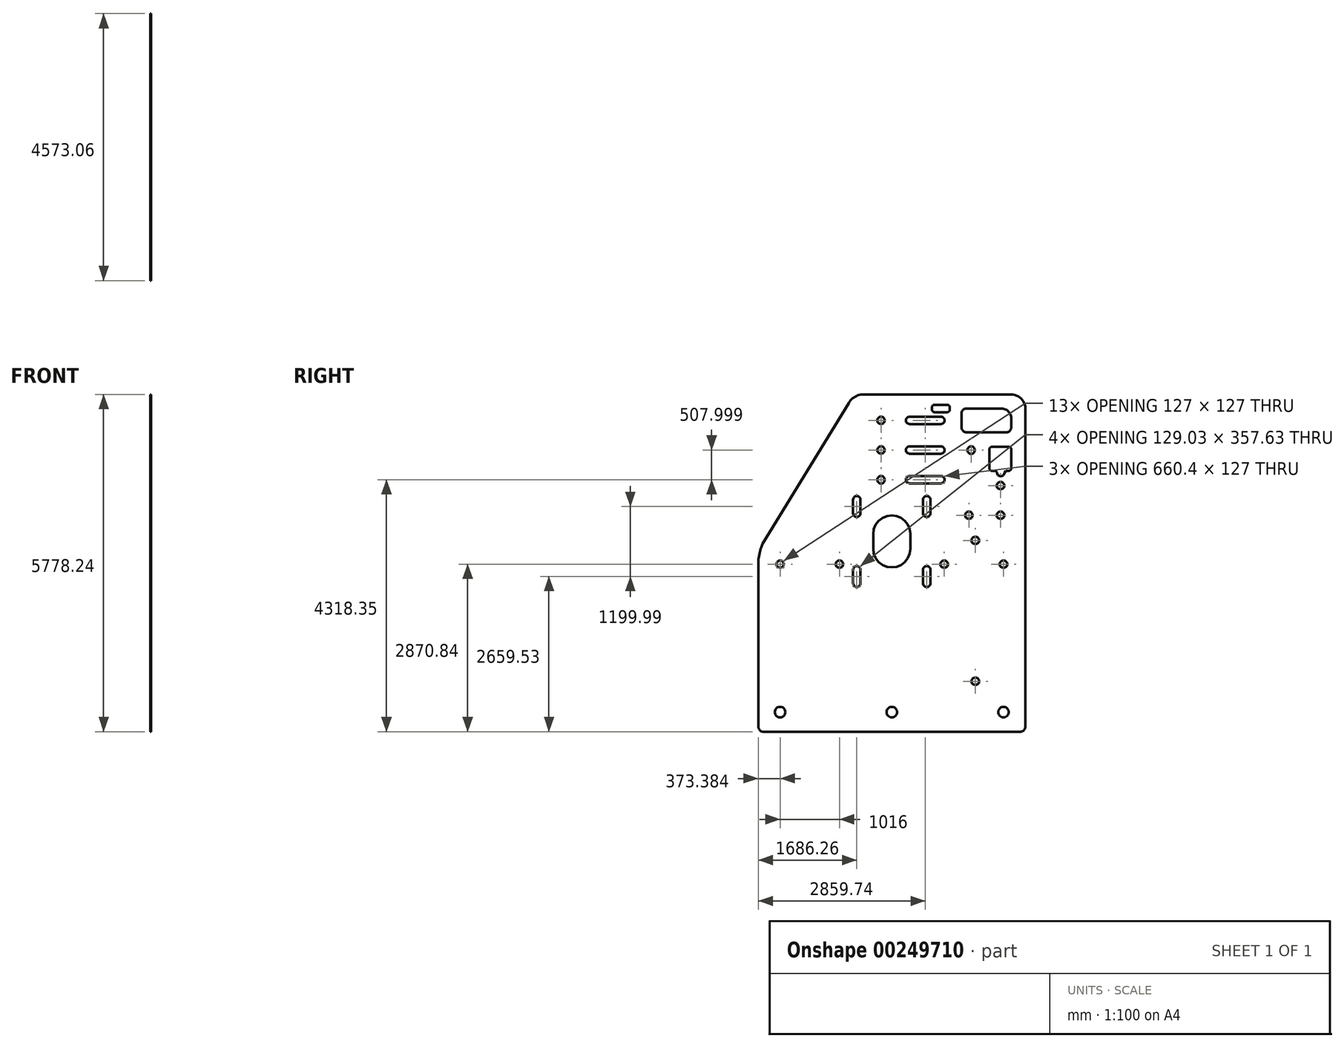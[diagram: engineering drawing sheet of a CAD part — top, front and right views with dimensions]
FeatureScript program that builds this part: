
annotation { "Feature Type Name" : "Feature", "Feature Type Description" : "" }
export const myFeature = defineFeature(function(context is Context, id is Id, definition is map)
    precondition{}
    {
        {
            var Q0;
            Q0=qCreatedBy(makeId("Right.planeOp"),FACE);
            var sketch = newSketch(context, id + "F0", { "sketchPlane" : qUnion([Q0])});
            skLineSegment(sketch, "E0", {"start": v(-705.3, 6120.73) * mm, "end": v(-698.95, 6105.42) * mm});
            skLineSegment(sketch, "E1", {"start": v(-603.87, 3290.42) * mm, "end": v(-593.78, 3277.27) * mm});
            skLineSegment(sketch, "E2", {"start": v(-617.02, 3190.53) * mm, "end": v(-632.33, 3184.18) * mm});
            skLineSegment(sketch, "E3", {"start": v(-648.77, 3182.02) * mm, "end": v(-665.2, 3184.18) * mm});
            skLineSegment(sketch, "E4", {"start": v(-593.78, 3277.27) * mm, "end": v(-587.43, 3261.96) * mm});
            skLineSegment(sketch, "E5", {"start": v(-665.2, 3306.86) * mm, "end": v(-648.77, 3309.02) * mm});
            skLineSegment(sketch, "E6", {"start": v(-710.1, 3229.09) * mm, "end": v(-712.27, 3245.52) * mm});
            skLineSegment(sketch, "E7", {"start": v(-2264.44, 6760.96) * mm, "end": v(-2248, 6758.8) * mm});
            skLineSegment(sketch, "E8", {"start": v(-2248, 6758.8) * mm, "end": v(-2232.7, 6752.45) * mm});
            skLineSegment(sketch, "E9", {"start": v(-693.67, 3290.42) * mm, "end": v(-680.52, 3300.51) * mm});
            skLineSegment(sketch, "E10", {"start": v(-710.1, 3261.96) * mm, "end": v(-703.76, 3277.27) * mm});
            skLineSegment(sketch, "E11", {"start": v(-603.87, 3200.62) * mm, "end": v(-617.02, 3190.53) * mm});
            skLineSegment(sketch, "E12", {"start": v(-617.02, 3300.51) * mm, "end": v(-603.87, 3290.42) * mm});
            skLineSegment(sketch, "E13", {"start": v(-648.77, 3309.02) * mm, "end": v(-632.33, 3306.86) * mm});
            skLineSegment(sketch, "E14", {"start": v(-2232.7, 6752.45) * mm, "end": v(-2219.54, 6742.36) * mm});
            skLineSegment(sketch, "E15", {"start": v(-665.2, 3184.18) * mm, "end": v(-680.52, 3190.53) * mm});
            skLineSegment(sketch, "E16", {"start": v(-2325.78, 6713.9) * mm, "end": v(-2319.44, 6729.2) * mm});
            skLineSegment(sketch, "E17", {"start": v(-2264.44, 6633.96) * mm, "end": v(-2280.88, 6636.12) * mm});
            skLineSegment(sketch, "E18", {"start": v(-2203.1, 6713.9) * mm, "end": v(-2200.94, 6697.46) * mm});
            skLineSegment(sketch, "E19", {"start": v(-693.67, 3200.62) * mm, "end": v(-703.76, 3213.77) * mm});
            skLineSegment(sketch, "E20", {"start": v(-2219.54, 6742.36) * mm, "end": v(-2209.45, 6729.2) * mm});
            skLineSegment(sketch, "E21", {"start": v(-2325.78, 6681.02) * mm, "end": v(-2327.94, 6697.46) * mm});
            skLineSegment(sketch, "E22", {"start": v(-585.27, 3245.52) * mm, "end": v(-587.43, 3229.09) * mm});
            skLineSegment(sketch, "E23", {"start": v(-2309.35, 6652.56) * mm, "end": v(-2319.44, 6665.7) * mm});
            skLineSegment(sketch, "E24", {"start": v(-2232.7, 6642.47) * mm, "end": v(-2248, 6636.12) * mm});
            skLineSegment(sketch, "E25", {"start": v(-698.95, 6105.42) * mm, "end": v(-696.79, 6088.98) * mm});
            skLineSegment(sketch, "E26", {"start": v(-680.52, 3190.53) * mm, "end": v(-693.67, 3200.62) * mm});
            skLineSegment(sketch, "E27", {"start": v(-703.76, 3277.27) * mm, "end": v(-693.67, 3290.42) * mm});
            skLineSegment(sketch, "E28", {"start": v(-587.43, 3261.96) * mm, "end": v(-585.27, 3245.52) * mm});
            skLineSegment(sketch, "E29", {"start": v(-632.33, 3306.86) * mm, "end": v(-617.02, 3300.51) * mm});
            skLineSegment(sketch, "E30", {"start": v(-712.27, 3245.52) * mm, "end": v(-710.1, 3261.96) * mm});
            skLineSegment(sketch, "E31", {"start": v(-2209.45, 6729.2) * mm, "end": v(-2203.1, 6713.9) * mm});
            skLineSegment(sketch, "E32", {"start": v(-703.76, 3213.77) * mm, "end": v(-710.1, 3229.09) * mm});
            skLineSegment(sketch, "E33", {"start": v(-680.52, 3300.51) * mm, "end": v(-665.2, 3306.86) * mm});
            skLineSegment(sketch, "E34", {"start": v(-587.43, 3229.09) * mm, "end": v(-593.78, 3213.77) * mm});
            skLineSegment(sketch, "E35", {"start": v(-632.33, 3184.18) * mm, "end": v(-648.77, 3182.02) * mm});
            skLineSegment(sketch, "E36", {"start": v(-2203.1, 6681.02) * mm, "end": v(-2209.45, 6665.7) * mm});
            skLineSegment(sketch, "E37", {"start": v(-660.44, 7189.1) * mm, "end": v(-666.79, 7173.79) * mm});
            skLineSegment(sketch, "E38", {"start": v(-783.12, 7221.97) * mm, "end": v(-776.77, 7237.29) * mm});
            skLineSegment(sketch, "E39", {"start": v(-2280.88, 6758.8) * mm, "end": v(-2264.44, 6760.96) * mm});
            skLineSegment(sketch, "E40", {"start": v(-676.88, 7250.44) * mm, "end": v(-666.79, 7237.29) * mm});
            skLineSegment(sketch, "E41", {"start": v(-753.53, 7150.55) * mm, "end": v(-766.68, 7160.64) * mm});
            skLineSegment(sketch, "E42", {"start": v(-721.78, 7269.04) * mm, "end": v(-705.34, 7266.88) * mm});
            skLineSegment(sketch, "E43", {"start": v(-776.77, 7173.79) * mm, "end": v(-783.12, 7189.1) * mm});
            skLineSegment(sketch, "E44", {"start": v(-738.21, 7266.88) * mm, "end": v(-721.78, 7269.04) * mm});
            skLineSegment(sketch, "E45", {"start": v(-2296.2, 6752.45) * mm, "end": v(-2280.88, 6758.8) * mm});
            skLineSegment(sketch, "E46", {"start": v(-2319.44, 6665.7) * mm, "end": v(-2325.78, 6681.02) * mm});
            skLineSegment(sketch, "E47", {"start": v(-2248, 6636.12) * mm, "end": v(-2264.44, 6633.96) * mm});
            skLineSegment(sketch, "E48", {"start": v(-666.79, 7173.79) * mm, "end": v(-676.88, 7160.64) * mm});
            skLineSegment(sketch, "E49", {"start": v(-271.96, 6057.23) * mm, "end": v(-278.3, 6072.55) * mm});
            skLineSegment(sketch, "E50", {"start": v(-766.68, 7250.44) * mm, "end": v(-753.53, 7260.53) * mm});
            skLineSegment(sketch, "E51", {"start": v(-2296.2, 6642.47) * mm, "end": v(-2309.35, 6652.56) * mm});
            skLineSegment(sketch, "E52", {"start": v(-2309.35, 6742.36) * mm, "end": v(-2296.2, 6752.45) * mm});
            skLineSegment(sketch, "E53", {"start": v(-2219.54, 6652.56) * mm, "end": v(-2232.7, 6642.47) * mm});
            skLineSegment(sketch, "E54", {"start": v(-2280.88, 6636.12) * mm, "end": v(-2296.2, 6642.47) * mm});
            skLineSegment(sketch, "E55", {"start": v(-705.34, 7144.2) * mm, "end": v(-721.78, 7142.04) * mm});
            skLineSegment(sketch, "E56", {"start": v(-783.12, 7189.1) * mm, "end": v(-785.28, 7205.54) * mm});
            skLineSegment(sketch, "E57", {"start": v(-660.44, 7221.97) * mm, "end": v(-658.28, 7205.54) * mm});
            skLineSegment(sketch, "E58", {"start": v(-2327.94, 6697.46) * mm, "end": v(-2325.78, 6713.9) * mm});
            skLineSegment(sketch, "E59", {"start": v(-776.77, 7237.29) * mm, "end": v(-766.68, 7250.44) * mm});
            skLineSegment(sketch, "E60", {"start": v(-666.79, 7237.29) * mm, "end": v(-660.44, 7221.97) * mm});
            skLineSegment(sketch, "E61", {"start": v(-690.03, 7150.55) * mm, "end": v(-705.34, 7144.2) * mm});
            skLineSegment(sketch, "E62", {"start": v(-2209.45, 6665.7) * mm, "end": v(-2219.54, 6652.56) * mm});
            skLineSegment(sketch, "E63", {"start": v(-676.88, 7160.64) * mm, "end": v(-690.03, 7150.55) * mm});
            skLineSegment(sketch, "E64", {"start": v(-785.28, 7205.54) * mm, "end": v(-783.12, 7221.97) * mm});
            skLineSegment(sketch, "E65", {"start": v(-233.4, 6150.32) * mm, "end": v(-216.97, 6152.48) * mm});
            skLineSegment(sketch, "E66", {"start": v(-2319.44, 6729.2) * mm, "end": v(-2309.35, 6742.36) * mm});
            skLineSegment(sketch, "E67", {"start": v(-2200.94, 6697.46) * mm, "end": v(-2203.1, 6681.02) * mm});
            skLineSegment(sketch, "E68", {"start": v(-658.28, 7205.54) * mm, "end": v(-660.44, 7189.1) * mm});
            skLineSegment(sketch, "E69", {"start": v(-280.47, 6088.98) * mm, "end": v(-278.3, 6105.42) * mm});
            skLineSegment(sketch, "E70", {"start": v(-261.87, 6044.08) * mm, "end": v(-271.96, 6057.23) * mm});
            skLineSegment(sketch, "E71", {"start": v(-216.97, 6152.48) * mm, "end": v(-200.53, 6150.32) * mm});
            skLineSegment(sketch, "E72", {"start": v(-153.47, 6088.98) * mm, "end": v(-155.63, 6072.55) * mm});
            skLineSegment(sketch, "E73", {"start": v(-155.63, 6072.55) * mm, "end": v(-161.98, 6057.23) * mm});
            skLineSegment(sketch, "E74", {"start": v(-766.68, 7160.64) * mm, "end": v(-776.77, 7173.79) * mm});
            skLineSegment(sketch, "E75", {"start": v(-161.98, 6120.73) * mm, "end": v(-155.63, 6105.42) * mm});
            skLineSegment(sketch, "E76", {"start": v(-738.21, 7144.2) * mm, "end": v(-753.53, 7150.55) * mm});
            skLineSegment(sketch, "E77", {"start": v(-278.3, 6072.55) * mm, "end": v(-280.47, 6088.98) * mm});
            skLineSegment(sketch, "E78", {"start": v(-278.3, 6105.42) * mm, "end": v(-271.96, 6120.73) * mm});
            skLineSegment(sketch, "E79", {"start": v(-248.72, 6034) * mm, "end": v(-261.87, 6044.08) * mm});
            skLineSegment(sketch, "E80", {"start": v(-248.72, 6143.98) * mm, "end": v(-233.4, 6150.32) * mm});
            skLineSegment(sketch, "E81", {"start": v(-216.97, 6533.48) * mm, "end": v(-233.4, 6535.65) * mm});
            skLineSegment(sketch, "E82", {"start": v(-155.63, 6105.42) * mm, "end": v(-153.47, 6088.98) * mm});
            skLineSegment(sketch, "E83", {"start": v(-161.98, 6057.23) * mm, "end": v(-172.07, 6044.08) * mm});
            skLineSegment(sketch, "E84", {"start": v(-185.22, 6034) * mm, "end": v(-200.53, 6027.65) * mm});
            skLineSegment(sketch, "E85", {"start": v(-721.78, 7142.04) * mm, "end": v(-738.21, 7144.2) * mm});
            skLineSegment(sketch, "E86", {"start": v(-185.22, 6542) * mm, "end": v(-200.53, 6535.65) * mm});
            skLineSegment(sketch, "E87", {"start": v(-172.07, 6552.08) * mm, "end": v(-185.22, 6542) * mm});
            skLineSegment(sketch, "E88", {"start": v(-200.53, 6027.65) * mm, "end": v(-216.97, 6025.48) * mm});
            skLineSegment(sketch, "E89", {"start": v(-233.4, 6027.65) * mm, "end": v(-248.72, 6034) * mm});
            skLineSegment(sketch, "E90", {"start": v(-172.07, 6133.89) * mm, "end": v(-161.98, 6120.73) * mm});
            skLineSegment(sketch, "E91", {"start": v(-200.53, 6535.65) * mm, "end": v(-216.97, 6533.48) * mm});
            skLineSegment(sketch, "E92", {"start": v(-172.07, 6044.08) * mm, "end": v(-185.22, 6034) * mm});
            skLineSegment(sketch, "E93", {"start": v(-753.53, 7260.53) * mm, "end": v(-738.21, 7266.88) * mm});
            skLineSegment(sketch, "E94", {"start": v(-261.87, 6133.89) * mm, "end": v(-248.72, 6143.98) * mm});
            skLineSegment(sketch, "E95", {"start": v(-690.03, 7260.53) * mm, "end": v(-676.88, 7250.44) * mm});
            skLineSegment(sketch, "E96", {"start": v(-705.34, 7266.88) * mm, "end": v(-690.03, 7260.53) * mm});
            skLineSegment(sketch, "E97", {"start": v(-200.53, 6150.32) * mm, "end": v(-185.22, 6143.98) * mm});
            skLineSegment(sketch, "E98", {"start": v(-185.22, 6651.98) * mm, "end": v(-172.07, 6641.89) * mm});
            skLineSegment(sketch, "E99", {"start": v(-261.87, 6641.89) * mm, "end": v(-248.72, 6651.98) * mm});
            skLineSegment(sketch, "E100", {"start": v(-172.07, 6641.89) * mm, "end": v(-161.98, 6628.73) * mm});
            skLineSegment(sketch, "E101", {"start": v(-44.72, 7552.16) * mm, "end": v(-50.51, 7543.5) * mm});
            skLineSegment(sketch, "E102", {"start": v(-261.87, 6552.08) * mm, "end": v(-271.96, 6565.23) * mm});
            skLineSegment(sketch, "E103", {"start": v(-216.97, 6660.48) * mm, "end": v(-200.53, 6658.32) * mm});
            skLineSegment(sketch, "E104", {"start": v(-50.51, 7543.5) * mm, "end": v(-57.38, 7535.66) * mm});
            skLineSegment(sketch, "E105", {"start": v(-216.97, 6025.48) * mm, "end": v(-233.4, 6027.65) * mm});
            skLineSegment(sketch, "E106", {"start": v(-161.98, 6628.73) * mm, "end": v(-155.63, 6613.42) * mm});
            skLineSegment(sketch, "E107", {"start": v(-83.23, 7518.4) * mm, "end": v(-93.1, 7515.05) * mm});
            skLineSegment(sketch, "E108", {"start": v(-271.96, 6628.73) * mm, "end": v(-261.87, 6641.89) * mm});
            skLineSegment(sketch, "E109", {"start": v(-153.47, 6596.98) * mm, "end": v(-155.63, 6580.55) * mm});
            skLineSegment(sketch, "E110", {"start": v(-103.31, 7513.01) * mm, "end": v(-113.7, 7512.33) * mm});
            skLineSegment(sketch, "E111", {"start": v(-113.7, 7512.33) * mm, "end": v(-805.3, 7512.33) * mm});
            skLineSegment(sketch, "E112", {"start": v(-40.12, 7561.5) * mm, "end": v(-44.72, 7552.16) * mm});
            skLineSegment(sketch, "E113", {"start": v(-161.98, 6565.23) * mm, "end": v(-172.07, 6552.08) * mm});
            skLineSegment(sketch, "E114", {"start": v(-65.22, 7528.8) * mm, "end": v(-73.88, 7523) * mm});
            skLineSegment(sketch, "E115", {"start": v(-36.77, 7571.37) * mm, "end": v(-40.12, 7561.5) * mm});
            skLineSegment(sketch, "E116", {"start": v(-271.96, 6565.23) * mm, "end": v(-278.3, 6580.55) * mm});
            skLineSegment(sketch, "E117", {"start": v(-73.88, 7523) * mm, "end": v(-83.23, 7518.4) * mm});
            skLineSegment(sketch, "E118", {"start": v(-155.63, 6613.42) * mm, "end": v(-153.47, 6596.98) * mm});
            skLineSegment(sketch, "E119", {"start": v(-34.73, 7581.59) * mm, "end": v(-36.77, 7571.37) * mm});
            skLineSegment(sketch, "E120", {"start": v(-57.38, 7535.66) * mm, "end": v(-65.22, 7528.8) * mm});
            skLineSegment(sketch, "E121", {"start": v(-200.53, 6658.32) * mm, "end": v(-185.22, 6651.98) * mm});
            skLineSegment(sketch, "E122", {"start": v(-155.63, 6580.55) * mm, "end": v(-161.98, 6565.23) * mm});
            skLineSegment(sketch, "E123", {"start": v(-248.72, 6651.98) * mm, "end": v(-233.4, 6658.32) * mm});
            skLineSegment(sketch, "E124", {"start": v(-93.1, 7515.05) * mm, "end": v(-103.31, 7513.01) * mm});
            skLineSegment(sketch, "E125", {"start": v(-233.4, 6658.32) * mm, "end": v(-216.97, 6660.48) * mm});
            skLineSegment(sketch, "E126", {"start": v(-185.22, 6143.98) * mm, "end": v(-172.07, 6133.89) * mm});
            skLineSegment(sketch, "E127", {"start": v(-248.72, 6542) * mm, "end": v(-261.87, 6552.08) * mm});
            skLineSegment(sketch, "E128", {"start": v(-233.4, 6535.65) * mm, "end": v(-248.72, 6542) * mm});
            skLineSegment(sketch, "E129", {"start": v(-278.3, 6613.42) * mm, "end": v(-271.96, 6628.73) * mm});
            skLineSegment(sketch, "E130", {"start": v(-280.47, 6596.98) * mm, "end": v(-278.3, 6613.42) * mm});
            skLineSegment(sketch, "E131", {"start": v(-278.3, 6580.55) * mm, "end": v(-280.47, 6596.98) * mm});
            skLineSegment(sketch, "E132", {"start": v(-34.05, 7749.15) * mm, "end": v(-34.05, 7591.99) * mm});
            skLineSegment(sketch, "E133", {"start": v(-46.9, 7813.78) * mm, "end": v(-39.8, 7792.87) * mm});
            skLineSegment(sketch, "E134", {"start": v(-56.68, 7833.6) * mm, "end": v(-46.9, 7813.78) * mm});
            skLineSegment(sketch, "E135", {"start": v(-874.28, 7552.16) * mm, "end": v(-868.5, 7543.5) * mm});
            skLineSegment(sketch, "E136", {"start": v(-34.05, 7591.99) * mm, "end": v(-34.73, 7581.59) * mm});
            skLineSegment(sketch, "E137", {"start": v(-868.5, 7886.88) * mm, "end": v(-861.62, 7894.71) * mm});
            skLineSegment(sketch, "E138", {"start": v(-853.79, 7901.58) * mm, "end": v(-845.13, 7907.37) * mm});
            skLineSegment(sketch, "E139", {"start": v(-118.5, 7895.42) * mm, "end": v(-100.13, 7883.14) * mm});
            skLineSegment(sketch, "E140", {"start": v(-868.5, 7543.5) * mm, "end": v(-861.62, 7535.66) * mm});
            skLineSegment(sketch, "E141", {"start": v(-882.24, 7859) * mm, "end": v(-878.89, 7868.87) * mm});
            skLineSegment(sketch, "E142", {"start": v(-835.78, 7518.4) * mm, "end": v(-825.91, 7515.05) * mm});
            skLineSegment(sketch, "E143", {"start": v(-825.91, 7515.05) * mm, "end": v(-815.7, 7513.01) * mm});
            skLineSegment(sketch, "E144", {"start": v(-815.7, 7513.01) * mm, "end": v(-805.3, 7512.33) * mm});
            skLineSegment(sketch, "E145", {"start": v(-138.31, 7905.19) * mm, "end": v(-118.5, 7895.42) * mm});
            skLineSegment(sketch, "E146", {"start": v(-845.13, 7907.37) * mm, "end": v(-835.78, 7911.98) * mm});
            skLineSegment(sketch, "E147", {"start": v(-83.52, 7868.58) * mm, "end": v(-68.95, 7851.97) * mm});
            skLineSegment(sketch, "E148", {"start": v(-35.5, 7771.2) * mm, "end": v(-34.05, 7749.15) * mm});
            skLineSegment(sketch, "E149", {"start": v(-853.79, 7528.8) * mm, "end": v(-845.13, 7523) * mm});
            skLineSegment(sketch, "E150", {"start": v(-202.94, 7918.04) * mm, "end": v(-180.9, 7916.6) * mm});
            skLineSegment(sketch, "E151", {"start": v(-861.62, 7535.66) * mm, "end": v(-853.79, 7528.8) * mm});
            skLineSegment(sketch, "E152", {"start": v(-68.95, 7851.97) * mm, "end": v(-56.68, 7833.6) * mm});
            skLineSegment(sketch, "E153", {"start": v(-884.95, 7591.99) * mm, "end": v(-884.95, 7838.39) * mm});
            skLineSegment(sketch, "E154", {"start": v(-815.7, 7917.36) * mm, "end": v(-805.3, 7918.04) * mm});
            skLineSegment(sketch, "E155", {"start": v(-100.13, 7883.14) * mm, "end": v(-83.52, 7868.58) * mm});
            skLineSegment(sketch, "E156", {"start": v(-825.91, 7915.33) * mm, "end": v(-815.7, 7917.36) * mm});
            skLineSegment(sketch, "E157", {"start": v(-878.89, 7868.87) * mm, "end": v(-874.28, 7878.21) * mm});
            skLineSegment(sketch, "E158", {"start": v(-180.9, 7916.6) * mm, "end": v(-159.23, 7912.29) * mm});
            skLineSegment(sketch, "E159", {"start": v(-845.13, 7523) * mm, "end": v(-835.78, 7518.4) * mm});
            skLineSegment(sketch, "E160", {"start": v(-884.95, 7838.39) * mm, "end": v(-884.27, 7848.78) * mm});
            skLineSegment(sketch, "E161", {"start": v(-861.62, 7894.71) * mm, "end": v(-853.79, 7901.58) * mm});
            skLineSegment(sketch, "E162", {"start": v(-159.23, 7912.29) * mm, "end": v(-138.31, 7905.19) * mm});
            skLineSegment(sketch, "E163", {"start": v(-805.3, 7918.04) * mm, "end": v(-202.94, 7918.04) * mm});
            skLineSegment(sketch, "E164", {"start": v(-712.27, 5658.52) * mm, "end": v(-710.1, 5674.96) * mm});
            skLineSegment(sketch, "E165", {"start": v(-39.8, 7792.87) * mm, "end": v(-35.5, 7771.2) * mm});
            skLineSegment(sketch, "E166", {"start": v(-835.78, 7911.98) * mm, "end": v(-825.91, 7915.33) * mm});
            skLineSegment(sketch, "E167", {"start": v(-693.67, 5703.42) * mm, "end": v(-680.52, 5713.51) * mm});
            skLineSegment(sketch, "E168", {"start": v(-603.87, 5613.62) * mm, "end": v(-617.02, 5603.53) * mm});
            skLineSegment(sketch, "E169", {"start": v(-632.33, 5719.86) * mm, "end": v(-617.02, 5713.51) * mm});
            skLineSegment(sketch, "E170", {"start": v(-665.2, 5597.18) * mm, "end": v(-680.52, 5603.53) * mm});
            skLineSegment(sketch, "E171", {"start": v(-710.1, 5642.09) * mm, "end": v(-712.27, 5658.52) * mm});
            skLineSegment(sketch, "E172", {"start": v(-703.76, 5626.77) * mm, "end": v(-710.1, 5642.09) * mm});
            skLineSegment(sketch, "E173", {"start": v(-878.89, 7561.5) * mm, "end": v(-874.28, 7552.16) * mm});
            skLineSegment(sketch, "E174", {"start": v(-617.02, 5603.53) * mm, "end": v(-632.33, 5597.18) * mm});
            skLineSegment(sketch, "E175", {"start": v(-710.1, 5674.96) * mm, "end": v(-703.76, 5690.27) * mm});
            skLineSegment(sketch, "E176", {"start": v(-665.2, 5719.86) * mm, "end": v(-648.77, 5722.02) * mm});
            skLineSegment(sketch, "E177", {"start": v(-648.77, 5595.02) * mm, "end": v(-665.2, 5597.18) * mm});
            skLineSegment(sketch, "E178", {"start": v(-884.27, 7581.59) * mm, "end": v(-882.24, 7571.37) * mm});
            skLineSegment(sketch, "E179", {"start": v(-874.28, 7878.21) * mm, "end": v(-868.5, 7886.88) * mm});
            skLineSegment(sketch, "E180", {"start": v(-882.24, 7571.37) * mm, "end": v(-878.89, 7561.5) * mm});
            skLineSegment(sketch, "E181", {"start": v(-593.78, 5690.27) * mm, "end": v(-587.43, 5674.96) * mm});
            skLineSegment(sketch, "E182", {"start": v(-587.43, 5642.09) * mm, "end": v(-593.78, 5626.77) * mm});
            skLineSegment(sketch, "E183", {"start": v(-587.43, 5674.96) * mm, "end": v(-585.27, 5658.52) * mm});
            skLineSegment(sketch, "E184", {"start": v(-632.33, 5597.18) * mm, "end": v(-648.77, 5595.02) * mm});
            skLineSegment(sketch, "E185", {"start": v(-884.27, 7848.78) * mm, "end": v(-882.24, 7859) * mm});
            skLineSegment(sketch, "E186", {"start": v(-680.52, 5603.53) * mm, "end": v(-693.67, 5613.62) * mm});
            skLineSegment(sketch, "E187", {"start": v(-680.52, 5713.51) * mm, "end": v(-665.2, 5719.86) * mm});
            skLineSegment(sketch, "E188", {"start": v(-648.77, 5722.02) * mm, "end": v(-632.33, 5719.86) * mm});
            skLineSegment(sketch, "E189", {"start": v(-585.27, 5658.52) * mm, "end": v(-587.43, 5642.09) * mm});
            skLineSegment(sketch, "E190", {"start": v(-617.02, 5713.51) * mm, "end": v(-603.87, 5703.42) * mm});
            skLineSegment(sketch, "E191", {"start": v(-884.95, 7591.99) * mm, "end": v(-884.27, 7581.59) * mm});
            skLineSegment(sketch, "E192", {"start": v(-593.78, 5626.77) * mm, "end": v(-603.87, 5613.62) * mm});
            skLineSegment(sketch, "E193", {"start": v(-693.67, 5613.62) * mm, "end": v(-703.76, 5626.77) * mm});
            skLineSegment(sketch, "E194", {"start": v(-603.87, 5703.42) * mm, "end": v(-593.78, 5690.27) * mm});
            skLineSegment(sketch, "E195", {"start": v(-703.76, 5690.27) * mm, "end": v(-693.67, 5703.42) * mm});
            skLineSegment(sketch, "E196", {"start": v(-2280.88, 7653.37) * mm, "end": v(-2296.2, 7659.72) * mm});
            skLineSegment(sketch, "E197", {"start": v(-2248, 7776.05) * mm, "end": v(-2232.7, 7769.7) * mm});
            skLineSegment(sketch, "E198", {"start": v(-2264.44, 7778.2) * mm, "end": v(-2248, 7776.05) * mm});
            skLineSegment(sketch, "E199", {"start": v(-2219.54, 7669.8) * mm, "end": v(-2232.7, 7659.72) * mm});
            skLineSegment(sketch, "E200", {"start": v(-2232.7, 7769.7) * mm, "end": v(-2219.54, 7759.6) * mm});
            skLineSegment(sketch, "E201", {"start": v(-2325.78, 7698.27) * mm, "end": v(-2327.94, 7714.7) * mm});
            skLineSegment(sketch, "E202", {"start": v(-2296.2, 7659.72) * mm, "end": v(-2309.35, 7669.8) * mm});
            skLineSegment(sketch, "E203", {"start": v(-2280.88, 7776.05) * mm, "end": v(-2264.44, 7778.2) * mm});
            skLineSegment(sketch, "E204", {"start": v(-2203.1, 7698.27) * mm, "end": v(-2209.45, 7682.96) * mm});
            skLineSegment(sketch, "E205", {"start": v(-2309.35, 7669.8) * mm, "end": v(-2319.44, 7682.96) * mm});
            skLineSegment(sketch, "E206", {"start": v(-2209.45, 7746.46) * mm, "end": v(-2203.1, 7731.14) * mm});
            skLineSegment(sketch, "E207", {"start": v(-2309.35, 7251.6) * mm, "end": v(-2296.2, 7261.7) * mm});
            skLineSegment(sketch, "E208", {"start": v(-2327.94, 7714.7) * mm, "end": v(-2325.78, 7731.14) * mm});
            skLineSegment(sketch, "E209", {"start": v(-2325.78, 7190.27) * mm, "end": v(-2327.94, 7206.7) * mm});
            skLineSegment(sketch, "E210", {"start": v(-2280.88, 7268.05) * mm, "end": v(-2264.44, 7270.2) * mm});
            skLineSegment(sketch, "E211", {"start": v(-2296.2, 7151.72) * mm, "end": v(-2309.35, 7161.8) * mm});
            skLineSegment(sketch, "E212", {"start": v(-2309.35, 7759.6) * mm, "end": v(-2296.2, 7769.7) * mm});
            skLineSegment(sketch, "E213", {"start": v(-2232.7, 7659.72) * mm, "end": v(-2248, 7653.37) * mm});
            skLineSegment(sketch, "E214", {"start": v(-2325.78, 7223.14) * mm, "end": v(-2319.44, 7238.46) * mm});
            skLineSegment(sketch, "E215", {"start": v(-2319.44, 7682.96) * mm, "end": v(-2325.78, 7698.27) * mm});
            skLineSegment(sketch, "E216", {"start": v(-2264.44, 7651.2) * mm, "end": v(-2280.88, 7653.37) * mm});
            skLineSegment(sketch, "E217", {"start": v(-2264.44, 7143.2) * mm, "end": v(-2280.88, 7145.37) * mm});
            skLineSegment(sketch, "E218", {"start": v(-2200.94, 7714.7) * mm, "end": v(-2203.1, 7698.27) * mm});
            skLineSegment(sketch, "E219", {"start": v(-2248, 7145.37) * mm, "end": v(-2264.44, 7143.2) * mm});
            skLineSegment(sketch, "E220", {"start": v(-2296.2, 7769.7) * mm, "end": v(-2280.88, 7776.05) * mm});
            skLineSegment(sketch, "E221", {"start": v(-2203.1, 7731.14) * mm, "end": v(-2200.94, 7714.7) * mm});
            skLineSegment(sketch, "E222", {"start": v(-2209.45, 7682.96) * mm, "end": v(-2219.54, 7669.8) * mm});
            skLineSegment(sketch, "E223", {"start": v(-2325.78, 7731.14) * mm, "end": v(-2319.44, 7746.46) * mm});
            skLineSegment(sketch, "E224", {"start": v(-2248, 7653.37) * mm, "end": v(-2264.44, 7651.2) * mm});
            skLineSegment(sketch, "E225", {"start": v(-2319.44, 7746.46) * mm, "end": v(-2309.35, 7759.6) * mm});
            skLineSegment(sketch, "E226", {"start": v(-2219.54, 7759.6) * mm, "end": v(-2209.45, 7746.46) * mm});
            skLineSegment(sketch, "E227", {"start": v(-2280.88, 7145.37) * mm, "end": v(-2296.2, 7151.72) * mm});
            skLineSegment(sketch, "E228", {"start": v(-2744.06, 6354.93) * mm, "end": v(-2741.87, 6371.62) * mm});
            skLineSegment(sketch, "E229", {"start": v(-1525.17, 6080.7) * mm, "end": v(-1535.43, 6094.07) * mm});
            skLineSegment(sketch, "E230", {"start": v(-1433.94, 6080.7) * mm, "end": v(-1447.3, 6070.45) * mm});
            skLineSegment(sketch, "E231", {"start": v(-2200.94, 7206.7) * mm, "end": v(-2203.1, 7190.27) * mm});
            skLineSegment(sketch, "E232", {"start": v(-2319.44, 7238.46) * mm, "end": v(-2309.35, 7251.6) * mm});
            skLineSegment(sketch, "E233", {"start": v(-2744.06, 5154.93) * mm, "end": v(-2741.87, 5171.63) * mm});
            skLineSegment(sketch, "E234", {"start": v(-1496.25, 6417.24) * mm, "end": v(-1479.55, 6419.44) * mm});
            skLineSegment(sketch, "E235", {"start": v(-1544.07, 6126.33) * mm, "end": v(-1544.07, 6354.93) * mm});
            skLineSegment(sketch, "E236", {"start": v(-1541.87, 4909.63) * mm, "end": v(-1544.07, 4926.33) * mm});
            skLineSegment(sketch, "E237", {"start": v(-2309.35, 7161.8) * mm, "end": v(-2319.44, 7174.96) * mm});
            skLineSegment(sketch, "E238", {"start": v(-2232.7, 7151.72) * mm, "end": v(-2248, 7145.37) * mm});
            skLineSegment(sketch, "E239", {"start": v(-2209.45, 7238.46) * mm, "end": v(-2203.1, 7223.14) * mm});
            skLineSegment(sketch, "E240", {"start": v(-1479.55, 6061.81) * mm, "end": v(-1496.25, 6064) * mm});
            skLineSegment(sketch, "E241", {"start": v(-2232.7, 7261.7) * mm, "end": v(-2219.54, 7251.6) * mm});
            skLineSegment(sketch, "E242", {"start": v(-2296.2, 7261.7) * mm, "end": v(-2280.88, 7268.05) * mm});
            skLineSegment(sketch, "E243", {"start": v(-2203.1, 7223.14) * mm, "end": v(-2200.94, 7206.7) * mm});
            skLineSegment(sketch, "E244", {"start": v(-2327.94, 7206.7) * mm, "end": v(-2325.78, 7223.14) * mm});
            skLineSegment(sketch, "E245", {"start": v(-2319.44, 7174.96) * mm, "end": v(-2325.78, 7190.27) * mm});
            skLineSegment(sketch, "E246", {"start": v(-2662.85, 5217.25) * mm, "end": v(-2647.3, 5210.8) * mm});
            skLineSegment(sketch, "E247", {"start": v(-1447.3, 6070.45) * mm, "end": v(-1462.86, 6064) * mm});
            skLineSegment(sketch, "E248", {"start": v(-2744.06, 4926.33) * mm, "end": v(-2744.06, 5154.93) * mm});
            skLineSegment(sketch, "E249", {"start": v(-2623.68, 5187.19) * mm, "end": v(-2617.23, 5171.63) * mm});
            skLineSegment(sketch, "E250", {"start": v(-2219.54, 7251.6) * mm, "end": v(-2209.45, 7238.46) * mm});
            skLineSegment(sketch, "E251", {"start": v(-2647.3, 5210.8) * mm, "end": v(-2633.93, 5200.55) * mm});
            skLineSegment(sketch, "E252", {"start": v(-2248, 7268.05) * mm, "end": v(-2232.7, 7261.7) * mm});
            skLineSegment(sketch, "E253", {"start": v(-2617.23, 4909.63) * mm, "end": v(-2623.68, 4894.07) * mm});
            skLineSegment(sketch, "E254", {"start": v(-1541.87, 6371.62) * mm, "end": v(-1535.43, 6387.18) * mm});
            skLineSegment(sketch, "E255", {"start": v(-2264.44, 7270.2) * mm, "end": v(-2248, 7268.05) * mm});
            skLineSegment(sketch, "E256", {"start": v(-2735.42, 5187.19) * mm, "end": v(-2725.17, 5200.55) * mm});
            skLineSegment(sketch, "E257", {"start": v(-1433.94, 6400.55) * mm, "end": v(-1423.68, 6387.18) * mm});
            skLineSegment(sketch, "E258", {"start": v(-2725.17, 5200.55) * mm, "end": v(-2711.8, 5210.8) * mm});
            skLineSegment(sketch, "E259", {"start": v(-2711.8, 4870.46) * mm, "end": v(-2725.17, 4880.71) * mm});
            skLineSegment(sketch, "E260", {"start": v(-2617.23, 5171.63) * mm, "end": v(-2615.03, 5154.93) * mm});
            skLineSegment(sketch, "E261", {"start": v(-1462.86, 6064) * mm, "end": v(-1479.55, 6061.81) * mm});
            skLineSegment(sketch, "E262", {"start": v(-2725.17, 6400.55) * mm, "end": v(-2711.8, 6410.8) * mm});
            skLineSegment(sketch, "E263", {"start": v(-1462.86, 6417.24) * mm, "end": v(-1447.3, 6410.8) * mm});
            skLineSegment(sketch, "E264", {"start": v(-1415.04, 5154.93) * mm, "end": v(-1415.04, 4926.33) * mm});
            skLineSegment(sketch, "E265", {"start": v(-1511.81, 6410.8) * mm, "end": v(-1496.25, 6417.24) * mm});
            skLineSegment(sketch, "E266", {"start": v(-2696.25, 5217.25) * mm, "end": v(-2679.55, 5219.45) * mm});
            skLineSegment(sketch, "E267", {"start": v(-2725.17, 4880.71) * mm, "end": v(-2735.42, 4894.07) * mm});
            skLineSegment(sketch, "E268", {"start": v(-2679.55, 5219.45) * mm, "end": v(-2662.85, 5217.25) * mm});
            skLineSegment(sketch, "E269", {"start": v(-2238.56, 5238.47) * mm, "end": v(-2304.31, 5288.92) * mm});
            skLineSegment(sketch, "E270", {"start": v(-1415.04, 4926.33) * mm, "end": v(-1417.24, 4909.63) * mm});
            skLineSegment(sketch, "E271", {"start": v(-1417.24, 6371.62) * mm, "end": v(-1415.04, 6354.93) * mm});
            skLineSegment(sketch, "E272", {"start": v(-1535.43, 6387.18) * mm, "end": v(-1525.17, 6400.55) * mm});
            skLineSegment(sketch, "E273", {"start": v(-1525.17, 6400.55) * mm, "end": v(-1511.81, 6410.8) * mm});
            skLineSegment(sketch, "E274", {"start": v(-1417.24, 6109.63) * mm, "end": v(-1423.68, 6094.07) * mm});
            skLineSegment(sketch, "E275", {"start": v(-1496.25, 6064) * mm, "end": v(-1511.81, 6070.45) * mm});
            skLineSegment(sketch, "E276", {"start": v(-1541.87, 5171.63) * mm, "end": v(-1535.43, 5187.19) * mm});
            skLineSegment(sketch, "E277", {"start": v(-2161.98, 5206.75) * mm, "end": v(-2238.56, 5238.47) * mm});
            skLineSegment(sketch, "E278", {"start": v(-2647.3, 4870.46) * mm, "end": v(-2662.85, 4864.01) * mm});
            skLineSegment(sketch, "E279", {"start": v(-2679.55, 6419.44) * mm, "end": v(-2662.85, 6417.24) * mm});
            skLineSegment(sketch, "E280", {"start": v(-2679.55, 4861.82) * mm, "end": v(-2696.25, 4864.01) * mm});
            skLineSegment(sketch, "E281", {"start": v(-2741.87, 5171.63) * mm, "end": v(-2735.42, 5187.19) * mm});
            skLineSegment(sketch, "E282", {"start": v(-1544.07, 4926.33) * mm, "end": v(-1544.07, 5154.93) * mm});
            skLineSegment(sketch, "E283", {"start": v(-1511.81, 6070.45) * mm, "end": v(-1525.17, 6080.7) * mm});
            skLineSegment(sketch, "E284", {"start": v(-1479.55, 6419.44) * mm, "end": v(-1462.86, 6417.24) * mm});
            skLineSegment(sketch, "E285", {"start": v(-2662.85, 6417.24) * mm, "end": v(-2647.3, 6410.8) * mm});
            skLineSegment(sketch, "E286", {"start": v(-1415.04, 6126.33) * mm, "end": v(-1417.24, 6109.63) * mm});
            skLineSegment(sketch, "E287", {"start": v(-2741.87, 4909.63) * mm, "end": v(-2744.06, 4926.33) * mm});
            skLineSegment(sketch, "E288", {"start": v(-1535.43, 6094.07) * mm, "end": v(-1541.87, 6109.63) * mm});
            skLineSegment(sketch, "E289", {"start": v(-1447.3, 6410.8) * mm, "end": v(-1433.94, 6400.55) * mm});
            skLineSegment(sketch, "E290", {"start": v(-2711.8, 5210.8) * mm, "end": v(-2696.25, 5217.25) * mm});
            skLineSegment(sketch, "E291", {"start": v(-2662.85, 4864.01) * mm, "end": v(-2679.55, 4861.82) * mm});
            skLineSegment(sketch, "E292", {"start": v(-715.39, 6044.08) * mm, "end": v(-728.54, 6034) * mm});
            skLineSegment(sketch, "E293", {"start": v(-698.95, 6072.55) * mm, "end": v(-705.3, 6057.23) * mm});
            skLineSegment(sketch, "E294", {"start": v(-821.62, 6105.42) * mm, "end": v(-815.28, 6120.73) * mm});
            skLineSegment(sketch, "E295", {"start": v(-705.3, 6057.23) * mm, "end": v(-715.39, 6044.08) * mm});
            skLineSegment(sketch, "E296", {"start": v(-776.72, 6150.32) * mm, "end": v(-760.29, 6152.48) * mm});
            skLineSegment(sketch, "E297", {"start": v(-1535.43, 4894.07) * mm, "end": v(-1541.87, 4909.63) * mm});
            skLineSegment(sketch, "E298", {"start": v(-805.19, 6133.89) * mm, "end": v(-792.04, 6143.98) * mm});
            skLineSegment(sketch, "E299", {"start": v(-715.39, 6133.89) * mm, "end": v(-705.3, 6120.73) * mm});
            skLineSegment(sketch, "E300", {"start": v(-1544.07, 6354.93) * mm, "end": v(-1541.87, 6371.62) * mm});
            skLineSegment(sketch, "E301", {"start": v(-696.79, 6088.98) * mm, "end": v(-698.95, 6072.55) * mm});
            skLineSegment(sketch, "E302", {"start": v(-792.04, 6143.98) * mm, "end": v(-776.72, 6150.32) * mm});
            skLineSegment(sketch, "E303", {"start": v(-815.28, 6057.23) * mm, "end": v(-821.62, 6072.55) * mm});
            skLineSegment(sketch, "E304", {"start": v(-1423.68, 6094.07) * mm, "end": v(-1433.94, 6080.7) * mm});
            skLineSegment(sketch, "E305", {"start": v(-821.62, 6072.55) * mm, "end": v(-823.79, 6088.98) * mm});
            skLineSegment(sketch, "E306", {"start": v(-2397.3, 5767.43) * mm, "end": v(-2397.3, 5513.43) * mm});
            skLineSegment(sketch, "E307", {"start": v(-805.19, 6044.08) * mm, "end": v(-815.28, 6057.23) * mm});
            skLineSegment(sketch, "E308", {"start": v(-728.54, 6034) * mm, "end": v(-743.85, 6027.65) * mm});
            skLineSegment(sketch, "E309", {"start": v(-728.54, 6143.98) * mm, "end": v(-715.39, 6133.89) * mm});
            skLineSegment(sketch, "E310", {"start": v(-271.96, 6120.73) * mm, "end": v(-261.87, 6133.89) * mm});
            skLineSegment(sketch, "E311", {"start": v(-1525.17, 4880.71) * mm, "end": v(-1535.43, 4894.07) * mm});
            skLineSegment(sketch, "E312", {"start": v(-792.04, 6034) * mm, "end": v(-805.19, 6044.08) * mm});
            skLineSegment(sketch, "E313", {"start": v(-823.79, 6088.98) * mm, "end": v(-821.62, 6105.42) * mm});
            skLineSegment(sketch, "E314", {"start": v(-760.29, 6025.48) * mm, "end": v(-776.72, 6027.65) * mm});
            skLineSegment(sketch, "E315", {"start": v(-593.78, 3213.77) * mm, "end": v(-603.87, 3200.62) * mm});
            skLineSegment(sketch, "E316", {"start": v(-743.85, 6027.65) * mm, "end": v(-760.29, 6025.48) * mm});
            skLineSegment(sketch, "E317", {"start": v(-2735.42, 4894.07) * mm, "end": v(-2741.87, 4909.63) * mm});
            skLineSegment(sketch, "E318", {"start": v(-1479.55, 5219.45) * mm, "end": v(-1462.86, 5217.25) * mm});
            skLineSegment(sketch, "E319", {"start": v(-743.85, 6150.32) * mm, "end": v(-728.54, 6143.98) * mm});
            skLineSegment(sketch, "E320", {"start": v(-776.72, 6027.65) * mm, "end": v(-792.04, 6034) * mm});
            skLineSegment(sketch, "E321", {"start": v(-1415.04, 6354.93) * mm, "end": v(-1415.04, 6126.33) * mm});
            skLineSegment(sketch, "E322", {"start": v(-815.28, 6120.73) * mm, "end": v(-805.19, 6133.89) * mm});
            skLineSegment(sketch, "E323", {"start": v(-760.29, 6152.48) * mm, "end": v(-743.85, 6150.32) * mm});
            skLineSegment(sketch, "E324", {"start": v(-277.7, 6819.88) * mm, "end": v(-275.53, 6803.45) * mm});
            skLineSegment(sketch, "E325", {"start": v(-230.61, 6758.56) * mm, "end": v(-214.18, 6756.4) * mm});
            skLineSegment(sketch, "E326", {"start": v(-398.7, 6867.24) * mm, "end": v(-395.05, 6863.07) * mm});
            skLineSegment(sketch, "E327", {"start": v(-401.8, 7239.71) * mm, "end": v(-398.7, 7244.32) * mm});
            skLineSegment(sketch, "E328", {"start": v(-401.8, 6871.85) * mm, "end": v(-398.7, 6867.24) * mm});
            skLineSegment(sketch, "E329", {"start": v(-390.88, 6859.42) * mm, "end": v(-386.27, 6856.34) * mm});
            skLineSegment(sketch, "E330", {"start": v(-404.24, 7234.74) * mm, "end": v(-401.8, 7239.71) * mm});
            skLineSegment(sketch, "E331", {"start": v(-386.27, 7255.23) * mm, "end": v(-381.3, 7257.68) * mm});
            skLineSegment(sketch, "E332", {"start": v(-407.32, 7219.65) * mm, "end": v(-406.03, 7229.49) * mm});
            skLineSegment(sketch, "E333", {"start": v(-376.05, 6852.1) * mm, "end": v(-365.08, 6850.66) * mm});
            skLineSegment(sketch, "E334", {"start": v(-406.03, 7229.49) * mm, "end": v(-404.24, 7234.74) * mm});
            skLineSegment(sketch, "E335", {"start": v(-197.74, 6758.58) * mm, "end": v(-182.43, 6764.93) * mm});
            skLineSegment(sketch, "E336", {"start": v(-398.7, 7244.32) * mm, "end": v(-395.05, 7248.5) * mm});
            skLineSegment(sketch, "E337", {"start": v(-259.09, 6774.99) * mm, "end": v(-245.93, 6764.9) * mm});
            skLineSegment(sketch, "E338", {"start": v(-395.05, 7248.5) * mm, "end": v(-390.88, 7252.15) * mm});
            skLineSegment(sketch, "E339", {"start": v(-407.47, 6893.05) * mm, "end": v(-406.03, 6882.08) * mm});
            skLineSegment(sketch, "E340", {"start": v(-404.24, 6876.83) * mm, "end": v(-401.8, 6871.85) * mm});
            skLineSegment(sketch, "E341", {"start": v(-407.47, 6893.05) * mm, "end": v(-407.32, 7219.65) * mm});
            skLineSegment(sketch, "E342", {"start": v(-395.05, 6863.07) * mm, "end": v(-390.88, 6859.42) * mm});
            skLineSegment(sketch, "E343", {"start": v(-277.7, 6819.88) * mm, "end": v(-302.34, 6850.7) * mm});
            skLineSegment(sketch, "E344", {"start": v(-390.88, 7252.15) * mm, "end": v(-386.27, 7255.23) * mm});
            skLineSegment(sketch, "E345", {"start": v(-159.2, 6788.18) * mm, "end": v(-152.86, 6803.5) * mm});
            skLineSegment(sketch, "E346", {"start": v(-381.3, 6853.88) * mm, "end": v(-376.05, 6852.1) * mm});
            skLineSegment(sketch, "E347", {"start": v(-406.03, 6882.08) * mm, "end": v(-404.24, 6876.83) * mm});
            skLineSegment(sketch, "E348", {"start": v(-152.86, 6803.5) * mm, "end": v(-150.7, 6819.93) * mm});
            skLineSegment(sketch, "E349", {"start": v(-275.53, 6803.45) * mm, "end": v(-269.18, 6788.13) * mm});
            skLineSegment(sketch, "E350", {"start": v(-245.93, 6764.9) * mm, "end": v(-230.61, 6758.56) * mm});
            skLineSegment(sketch, "E351", {"start": v(-214.18, 6756.4) * mm, "end": v(-197.74, 6758.58) * mm});
            skLineSegment(sketch, "E352", {"start": v(-182.43, 6764.93) * mm, "end": v(-169.28, 6775.02) * mm});
            skLineSegment(sketch, "E353", {"start": v(-386.27, 6856.34) * mm, "end": v(-381.3, 6853.88) * mm});
            skLineSegment(sketch, "E354", {"start": v(-302.34, 6850.7) * mm, "end": v(-365.08, 6850.66) * mm});
            skLineSegment(sketch, "E355", {"start": v(-1817.68, 7670.55) * mm, "end": v(-1804.52, 7660.46) * mm});
            skLineSegment(sketch, "E356", {"start": v(-211.07, 5296.84) * mm, "end": v(-197.92, 5306.93) * mm});
            skLineSegment(sketch, "E357", {"start": v(-182.6, 5190.6) * mm, "end": v(-197.92, 5196.95) * mm});
            skLineSegment(sketch, "E358", {"start": v(-121.27, 5296.84) * mm, "end": v(-111.18, 5283.7) * mm});
            skLineSegment(sketch, "E359", {"start": v(-134.42, 5306.93) * mm, "end": v(-121.27, 5296.84) * mm});
            skLineSegment(sketch, "E360", {"start": v(-121.27, 5207.04) * mm, "end": v(-134.42, 5196.95) * mm});
            skLineSegment(sketch, "E361", {"start": v(-1836.27, 7715.45) * mm, "end": v(-1834.11, 7699.02) * mm});
            skLineSegment(sketch, "E362", {"start": v(-149.73, 5190.6) * mm, "end": v(-166.17, 5188.44) * mm});
            skLineSegment(sketch, "E363", {"start": v(-197.92, 5306.93) * mm, "end": v(-182.6, 5313.28) * mm});
            skLineSegment(sketch, "E364", {"start": v(-1827.77, 7683.7) * mm, "end": v(-1817.68, 7670.55) * mm});
            skLineSegment(sketch, "E365", {"start": v(-102.67, 5251.94) * mm, "end": v(-104.83, 5235.5) * mm});
            skLineSegment(sketch, "E366", {"start": v(-104.83, 5268.38) * mm, "end": v(-102.67, 5251.94) * mm});
            skLineSegment(sketch, "E367", {"start": v(-229.67, 5251.94) * mm, "end": v(-227.5, 5268.38) * mm});
            skLineSegment(sketch, "E368", {"start": v(-111.18, 5220.2) * mm, "end": v(-121.27, 5207.04) * mm});
            skLineSegment(sketch, "E369", {"start": v(-4357.66, 5365.92) * mm, "end": v(-4361.22, 5335.58) * mm});
            skLineSegment(sketch, "E370", {"start": v(-4347.52, 5426.16) * mm, "end": v(-4353.1, 5396.13) * mm});
            skLineSegment(sketch, "E371", {"start": v(-111.18, 5283.7) * mm, "end": v(-104.83, 5268.38) * mm});
            skLineSegment(sketch, "E372", {"start": v(-4361.22, 5335.58) * mm, "end": v(-4363.77, 5305.14) * mm});
            skLineSegment(sketch, "E373", {"start": v(-227.5, 5235.5) * mm, "end": v(-229.67, 5251.94) * mm});
            skLineSegment(sketch, "E374", {"start": v(-211.07, 5207.04) * mm, "end": v(-221.16, 5220.2) * mm});
            skLineSegment(sketch, "E375", {"start": v(-104.83, 5235.5) * mm, "end": v(-111.18, 5220.2) * mm});
            skLineSegment(sketch, "E376", {"start": v(-166.17, 5315.44) * mm, "end": v(-149.73, 5313.28) * mm});
            skLineSegment(sketch, "E377", {"start": v(-149.73, 5313.28) * mm, "end": v(-134.42, 5306.93) * mm});
            skLineSegment(sketch, "E378", {"start": v(-4353.1, 5396.13) * mm, "end": v(-4357.66, 5365.92) * mm});
            skLineSegment(sketch, "E379", {"start": v(-197.92, 5196.95) * mm, "end": v(-211.07, 5207.04) * mm});
            skLineSegment(sketch, "E380", {"start": v(-221.16, 5283.7) * mm, "end": v(-211.07, 5296.84) * mm});
            skLineSegment(sketch, "E381", {"start": v(-221.16, 5220.2) * mm, "end": v(-227.5, 5235.5) * mm});
            skLineSegment(sketch, "E382", {"start": v(-1834.11, 7699.02) * mm, "end": v(-1827.77, 7683.7) * mm});
            skLineSegment(sketch, "E383", {"start": v(-134.42, 5196.95) * mm, "end": v(-149.73, 5190.6) * mm});
            skLineSegment(sketch, "E384", {"start": v(-182.6, 5313.28) * mm, "end": v(-166.17, 5315.44) * mm});
            skLineSegment(sketch, "E385", {"start": v(-166.17, 5188.44) * mm, "end": v(-182.6, 5190.6) * mm});
            skLineSegment(sketch, "E386", {"start": v(-227.5, 5268.38) * mm, "end": v(-221.16, 5283.7) * mm});
            skLineSegment(sketch, "E387", {"start": v(204.3, 2444.4) * mm, "end": v(206.48, 2455.36) * mm});
            skLineSegment(sketch, "E388", {"start": v(121.8, 2381.1) * mm, "end": v(-4280.4, 2381.1) * mm});
            skLineSegment(sketch, "E389", {"start": v(154.48, 2387.6) * mm, "end": v(164.5, 2392.54) * mm});
            skLineSegment(sketch, "E390", {"start": v(189.56, 2414.52) * mm, "end": v(195.77, 2423.8) * mm});
            skLineSegment(sketch, "E391", {"start": v(195.77, 2423.8) * mm, "end": v(200.7, 2433.83) * mm});
            skLineSegment(sketch, "E392", {"start": v(205.15, 7945.88) * mm, "end": v(207.25, 7913.84) * mm});
            skLineSegment(sketch, "E393", {"start": v(-4348.16, 2414.52) * mm, "end": v(-4354.36, 2423.8) * mm});
            skLineSegment(sketch, "E394", {"start": v(198.88, 7977.38) * mm, "end": v(205.15, 7945.88) * mm});
            skLineSegment(sketch, "E395", {"start": v(-4362.9, 2444.4) * mm, "end": v(-4365.08, 2455.36) * mm});
            skLineSegment(sketch, "E396", {"start": v(-4365.08, 2455.36) * mm, "end": v(-4365.8, 2466.51) * mm});
            skLineSegment(sketch, "E397", {"start": v(206.48, 2455.36) * mm, "end": v(207.21, 2466.51) * mm});
            skLineSegment(sketch, "E398", {"start": v(-4340.79, 2406.12) * mm, "end": v(-4348.16, 2414.52) * mm});
            skLineSegment(sketch, "E399", {"start": v(143.9, 2384) * mm, "end": v(154.48, 2387.6) * mm});
            skLineSegment(sketch, "E400", {"start": v(207.25, 7913.84) * mm, "end": v(207.21, 2466.51) * mm});
            skLineSegment(sketch, "E401", {"start": v(188.56, 8007.79) * mm, "end": v(198.88, 7977.38) * mm});
            skLineSegment(sketch, "E402", {"start": v(174.36, 8036.59) * mm, "end": v(188.56, 8007.79) * mm});
            skLineSegment(sketch, "E403", {"start": v(-4363.77, 5305.14) * mm, "end": v(-4365.8, 5244.08) * mm});
            skLineSegment(sketch, "E404", {"start": v(132.94, 2381.83) * mm, "end": v(143.9, 2384) * mm});
            skLineSegment(sketch, "E405", {"start": v(-4365.8, 2466.51) * mm, "end": v(-4365.8, 5244.08) * mm});
            skLineSegment(sketch, "E406", {"start": v(182.2, 2406.12) * mm, "end": v(189.56, 2414.52) * mm});
            skLineSegment(sketch, "E407", {"start": v(-4332.39, 2398.75) * mm, "end": v(-4340.79, 2406.12) * mm});
            skLineSegment(sketch, "E408", {"start": v(200.7, 2433.83) * mm, "end": v(204.3, 2444.4) * mm});
            skLineSegment(sketch, "E409", {"start": v(-4359.3, 2433.83) * mm, "end": v(-4362.9, 2444.4) * mm});
            skLineSegment(sketch, "E410", {"start": v(-4313.08, 2387.6) * mm, "end": v(-4323.1, 2392.54) * mm});
            skLineSegment(sketch, "E411", {"start": v(-4280.4, 2381.1) * mm, "end": v(-4291.54, 2381.83) * mm});
            skLineSegment(sketch, "E412", {"start": v(-4302.5, 2384) * mm, "end": v(-4313.08, 2387.6) * mm});
            skLineSegment(sketch, "E413", {"start": v(-4323.1, 2392.54) * mm, "end": v(-4332.39, 2398.75) * mm});
            skLineSegment(sketch, "E414", {"start": v(121.8, 2381.1) * mm, "end": v(132.94, 2381.83) * mm});
            skLineSegment(sketch, "E415", {"start": v(-4354.36, 2423.8) * mm, "end": v(-4359.3, 2433.83) * mm});
            skLineSegment(sketch, "E416", {"start": v(-4291.54, 2381.83) * mm, "end": v(-4302.5, 2384) * mm});
            skLineSegment(sketch, "E417", {"start": v(164.5, 2392.54) * mm, "end": v(173.8, 2398.75) * mm});
            skLineSegment(sketch, "E418", {"start": v(173.8, 2398.75) * mm, "end": v(182.2, 2406.12) * mm});
            skLineSegment(sketch, "E419", {"start": v(-2659.44, 8141.82) * mm, "end": v(-2634.6, 8149.45) * mm});
            skLineSegment(sketch, "E420", {"start": v(-4340.94, 5456) * mm, "end": v(-4347.52, 5426.16) * mm});
            skLineSegment(sketch, "E421", {"start": v(-2817.84, 8013.5) * mm, "end": v(-2803.35, 8035.06) * mm});
            skLineSegment(sketch, "E422", {"start": v(-2960, 5313.28) * mm, "end": v(-2944.68, 5306.93) * mm});
            skLineSegment(sketch, "E423", {"start": v(55.7, 8140.65) * mm, "end": v(84.5, 8126.45) * mm});
            skLineSegment(sketch, "E424", {"start": v(-2634.6, 8149.45) * mm, "end": v(-2609.22, 8154.93) * mm});
            skLineSegment(sketch, "E425", {"start": v(-6.21, 8157.24) * mm, "end": v(25.29, 8150.98) * mm});
            skLineSegment(sketch, "E426", {"start": v(-4324.83, 5514.92) * mm, "end": v(-4333.38, 5485.6) * mm});
            skLineSegment(sketch, "E427", {"start": v(-2557.5, 8159.34) * mm, "end": v(-38.26, 8159.34) * mm});
            skLineSegment(sketch, "E428", {"start": v(111.2, 8108.6) * mm, "end": v(135.34, 8087.43) * mm});
            skLineSegment(sketch, "E429", {"start": v(-4293.38, 5600.97) * mm, "end": v(-2817.84, 8013.5) * mm});
            skLineSegment(sketch, "E430", {"start": v(-4293.38, 5600.97) * mm, "end": v(-4315.3, 5543.95) * mm});
            skLineSegment(sketch, "E431", {"start": v(-2931.52, 5296.84) * mm, "end": v(-2921.43, 5283.7) * mm});
            skLineSegment(sketch, "E432", {"start": v(156.52, 8063.3) * mm, "end": v(174.36, 8036.59) * mm});
            skLineSegment(sketch, "E433", {"start": v(-2728.8, 8106.75) * mm, "end": v(-2706.7, 8120.4) * mm});
            skLineSegment(sketch, "E434", {"start": v(-2921.43, 5283.7) * mm, "end": v(-2915.09, 5268.38) * mm});
            skLineSegment(sketch, "E435", {"start": v(-2915.09, 5268.38) * mm, "end": v(-2912.93, 5251.94) * mm});
            skLineSegment(sketch, "E436", {"start": v(-2749.67, 8091.28) * mm, "end": v(-2728.8, 8106.75) * mm});
            skLineSegment(sketch, "E437", {"start": v(-4315.3, 5543.95) * mm, "end": v(-4324.83, 5514.92) * mm});
            skLineSegment(sketch, "E438", {"start": v(-2787.07, 8055.3) * mm, "end": v(-2769.14, 8074.08) * mm});
            skLineSegment(sketch, "E439", {"start": v(-2944.68, 5306.93) * mm, "end": v(-2931.52, 5296.84) * mm});
            skLineSegment(sketch, "E440", {"start": v(84.5, 8126.45) * mm, "end": v(111.2, 8108.6) * mm});
            skLineSegment(sketch, "E441", {"start": v(-2583.46, 8158.24) * mm, "end": v(-2557.5, 8159.34) * mm});
            skLineSegment(sketch, "E442", {"start": v(-2803.35, 8035.06) * mm, "end": v(-2787.07, 8055.3) * mm});
            skLineSegment(sketch, "E443", {"start": v(-38.26, 8159.34) * mm, "end": v(-6.21, 8157.24) * mm});
            skLineSegment(sketch, "E444", {"start": v(-2683.53, 8132.12) * mm, "end": v(-2659.44, 8141.82) * mm});
            skLineSegment(sketch, "E445", {"start": v(135.34, 8087.43) * mm, "end": v(156.52, 8063.3) * mm});
            skLineSegment(sketch, "E446", {"start": v(25.29, 8150.98) * mm, "end": v(55.7, 8140.65) * mm});
            skLineSegment(sketch, "E447", {"start": v(-2769.14, 8074.08) * mm, "end": v(-2749.67, 8091.28) * mm});
            skLineSegment(sketch, "E448", {"start": v(-4333.38, 5485.6) * mm, "end": v(-4340.94, 5456) * mm});
            skLineSegment(sketch, "E449", {"start": v(-2609.22, 8154.93) * mm, "end": v(-2583.46, 8158.24) * mm});
            skLineSegment(sketch, "E450", {"start": v(-2706.7, 8120.4) * mm, "end": v(-2683.53, 8132.12) * mm});
            skLineSegment(sketch, "E451", {"start": v(-2912.93, 5251.94) * mm, "end": v(-2915.09, 5235.5) * mm});
            skLineSegment(sketch, "E452", {"start": v(-2915.09, 5235.5) * mm, "end": v(-2921.43, 5220.2) * mm});
            skLineSegment(sketch, "E453", {"start": v(-4070.92, 2671.71) * mm, "end": v(-4079.98, 2693.57) * mm});
            skLineSegment(sketch, "E454", {"start": v(-3992.43, 2807.67) * mm, "end": v(-3968.97, 2804.59) * mm});
            skLineSegment(sketch, "E455", {"start": v(-4070.92, 2762.35) * mm, "end": v(-4056.52, 2781.13) * mm});
            skLineSegment(sketch, "E456", {"start": v(-4083.07, 2717.03) * mm, "end": v(-4079.98, 2740.5) * mm});
            skLineSegment(sketch, "E457", {"start": v(-3968.97, 2804.59) * mm, "end": v(-3947.1, 2795.53) * mm});
            skLineSegment(sketch, "E458", {"start": v(-2931.52, 5207.04) * mm, "end": v(-2944.68, 5196.95) * mm});
            skLineSegment(sketch, "E459", {"start": v(-3031.42, 5220.2) * mm, "end": v(-3037.76, 5235.5) * mm});
            skLineSegment(sketch, "E460", {"start": v(-2976.43, 5188.44) * mm, "end": v(-2992.86, 5190.6) * mm});
            skLineSegment(sketch, "E461", {"start": v(-2992.86, 5190.6) * mm, "end": v(-3008.18, 5196.95) * mm});
            skLineSegment(sketch, "E462", {"start": v(-2944.68, 5196.95) * mm, "end": v(-2960, 5190.6) * mm});
            skLineSegment(sketch, "E463", {"start": v(-3037.76, 5235.5) * mm, "end": v(-3039.93, 5251.94) * mm});
            skLineSegment(sketch, "E464", {"start": v(-4056.52, 2652.94) * mm, "end": v(-4070.92, 2671.71) * mm});
            skLineSegment(sketch, "E465", {"start": v(-4079.98, 2693.57) * mm, "end": v(-4083.07, 2717.03) * mm});
            skLineSegment(sketch, "E466", {"start": v(-2921.43, 5220.2) * mm, "end": v(-2931.52, 5207.04) * mm});
            skLineSegment(sketch, "E467", {"start": v(-4056.52, 2781.13) * mm, "end": v(-4037.75, 2795.53) * mm});
            skLineSegment(sketch, "E468", {"start": v(-4015.89, 2804.59) * mm, "end": v(-3992.43, 2807.67) * mm});
            skLineSegment(sketch, "E469", {"start": v(-4037.75, 2638.54) * mm, "end": v(-4056.52, 2652.94) * mm});
            skLineSegment(sketch, "E470", {"start": v(-2976.43, 5315.44) * mm, "end": v(-2960, 5313.28) * mm});
            skLineSegment(sketch, "E471", {"start": v(-2960, 5190.6) * mm, "end": v(-2976.43, 5188.44) * mm});
            skLineSegment(sketch, "E472", {"start": v(-3039.93, 5251.94) * mm, "end": v(-3037.76, 5268.38) * mm});
            skLineSegment(sketch, "E473", {"start": v(-3008.18, 5196.95) * mm, "end": v(-3021.33, 5207.04) * mm});
            skLineSegment(sketch, "E474", {"start": v(-3031.42, 5283.7) * mm, "end": v(-3021.33, 5296.84) * mm});
            skLineSegment(sketch, "E475", {"start": v(-3021.33, 5296.84) * mm, "end": v(-3008.18, 5306.93) * mm});
            skLineSegment(sketch, "E476", {"start": v(-3037.76, 5268.38) * mm, "end": v(-3031.42, 5283.7) * mm});
            skLineSegment(sketch, "E477", {"start": v(-2992.86, 5313.28) * mm, "end": v(-2976.43, 5315.44) * mm});
            skLineSegment(sketch, "E478", {"start": v(-3021.33, 5207.04) * mm, "end": v(-3031.42, 5220.2) * mm});
            skLineSegment(sketch, "E479", {"start": v(-3008.18, 5306.93) * mm, "end": v(-2992.86, 5313.28) * mm});
            skLineSegment(sketch, "E480", {"start": v(-4015.89, 2629.48) * mm, "end": v(-4037.75, 2638.54) * mm});
            skLineSegment(sketch, "E481", {"start": v(-4079.98, 2740.5) * mm, "end": v(-4070.92, 2762.35) * mm});
            skLineSegment(sketch, "E482", {"start": v(-4037.75, 2795.53) * mm, "end": v(-4015.89, 2804.59) * mm});
            skLineSegment(sketch, "E483", {"start": v(-3960.68, 5196.95) * mm, "end": v(-3976, 5190.6) * mm});
            skLineSegment(sketch, "E484", {"start": v(-3947.1, 2795.53) * mm, "end": v(-3928.33, 2781.13) * mm});
            skLineSegment(sketch, "E485", {"start": v(-3913.93, 2762.35) * mm, "end": v(-3904.87, 2740.5) * mm});
            skLineSegment(sketch, "E486", {"start": v(-3904.87, 2693.57) * mm, "end": v(-3913.93, 2671.71) * mm});
            skLineSegment(sketch, "E487", {"start": v(-3947.52, 5296.84) * mm, "end": v(-3937.43, 5283.7) * mm});
            skLineSegment(sketch, "E488", {"start": v(-3937.43, 5220.2) * mm, "end": v(-3947.52, 5207.04) * mm});
            skLineSegment(sketch, "E489", {"start": v(-3928.33, 2781.13) * mm, "end": v(-3913.93, 2762.35) * mm});
            skLineSegment(sketch, "E490", {"start": v(-3992.43, 2626.4) * mm, "end": v(-4015.89, 2629.48) * mm});
            skLineSegment(sketch, "E491", {"start": v(-4053.76, 5268.38) * mm, "end": v(-4047.42, 5283.7) * mm});
            skLineSegment(sketch, "E492", {"start": v(-3968.97, 2629.48) * mm, "end": v(-3992.43, 2626.4) * mm});
            skLineSegment(sketch, "E493", {"start": v(-3947.52, 5207.04) * mm, "end": v(-3960.68, 5196.95) * mm});
            skLineSegment(sketch, "E494", {"start": v(-4047.42, 5283.7) * mm, "end": v(-4037.33, 5296.84) * mm});
            skLineSegment(sketch, "E495", {"start": v(-3976, 5190.6) * mm, "end": v(-3992.43, 5188.44) * mm});
            skLineSegment(sketch, "E496", {"start": v(-3901.79, 2717.03) * mm, "end": v(-3904.87, 2693.57) * mm});
            skLineSegment(sketch, "E497", {"start": v(-4024.18, 5196.95) * mm, "end": v(-4037.33, 5207.04) * mm});
            skLineSegment(sketch, "E498", {"start": v(-3992.43, 5188.44) * mm, "end": v(-4008.86, 5190.6) * mm});
            skLineSegment(sketch, "E499", {"start": v(-3913.93, 2671.71) * mm, "end": v(-3928.33, 2652.94) * mm});
            skLineSegment(sketch, "E500", {"start": v(-3947.1, 2638.54) * mm, "end": v(-3968.97, 2629.48) * mm});
            skLineSegment(sketch, "E501", {"start": v(-3928.33, 2652.94) * mm, "end": v(-3947.1, 2638.54) * mm});
            skLineSegment(sketch, "E502", {"start": v(-4055.93, 5251.94) * mm, "end": v(-4053.76, 5268.38) * mm});
            skLineSegment(sketch, "E503", {"start": v(-4037.33, 5296.84) * mm, "end": v(-4024.18, 5306.93) * mm});
            skLineSegment(sketch, "E504", {"start": v(-4008.86, 5190.6) * mm, "end": v(-4024.18, 5196.95) * mm});
            skLineSegment(sketch, "E505", {"start": v(-3904.87, 2740.5) * mm, "end": v(-3901.79, 2717.03) * mm});
            skLineSegment(sketch, "E506", {"start": v(-4008.86, 5313.28) * mm, "end": v(-3992.43, 5315.44) * mm});
            skLineSegment(sketch, "E507", {"start": v(-3992.43, 5315.44) * mm, "end": v(-3976, 5313.28) * mm});
            skLineSegment(sketch, "E508", {"start": v(-3960.68, 5306.93) * mm, "end": v(-3947.52, 5296.84) * mm});
            skLineSegment(sketch, "E509", {"start": v(-4024.18, 5306.93) * mm, "end": v(-4008.86, 5313.28) * mm});
            skLineSegment(sketch, "E510", {"start": v(-3976, 5313.28) * mm, "end": v(-3960.68, 5306.93) * mm});
            skLineSegment(sketch, "E511", {"start": v(-3937.43, 5283.7) * mm, "end": v(-3931.09, 5268.38) * mm});
            skLineSegment(sketch, "E512", {"start": v(-3931.09, 5268.38) * mm, "end": v(-3928.93, 5251.94) * mm});
            skLineSegment(sketch, "E513", {"start": v(-3928.93, 5251.94) * mm, "end": v(-3931.09, 5235.5) * mm});
            skLineSegment(sketch, "E514", {"start": v(-3931.09, 5235.5) * mm, "end": v(-3937.43, 5220.2) * mm});
            skLineSegment(sketch, "E515", {"start": v(-34.05, 6887.52) * mm, "end": v(-35.13, 6882.08) * mm});
            skLineSegment(sketch, "E516", {"start": v(-39.37, 6871.85) * mm, "end": v(-42.45, 6867.24) * mm});
            skLineSegment(sketch, "E517", {"start": v(-35.13, 6882.08) * mm, "end": v(-36.92, 6876.83) * mm});
            skLineSegment(sketch, "E518", {"start": v(-50.28, 7252.15) * mm, "end": v(-54.89, 7255.23) * mm});
            skLineSegment(sketch, "E519", {"start": v(-36.92, 6876.83) * mm, "end": v(-39.37, 6871.85) * mm});
            skLineSegment(sketch, "E520", {"start": v(-381.3, 7257.68) * mm, "end": v(-376.05, 7259.46) * mm});
            skLineSegment(sketch, "E521", {"start": v(-59.86, 6853.88) * mm, "end": v(-65.11, 6852.1) * mm});
            skLineSegment(sketch, "E522", {"start": v(-1988.66, 2717.03) * mm, "end": v(-1991.75, 2693.57) * mm});
            skLineSegment(sketch, "E523", {"start": v(-34.05, 7224.05) * mm, "end": v(-35.13, 7229.49) * mm});
            skLineSegment(sketch, "E524", {"start": v(-39.37, 7239.71) * mm, "end": v(-42.45, 7244.32) * mm});
            skLineSegment(sketch, "E525", {"start": v(-1991.75, 2740.5) * mm, "end": v(-1988.66, 2717.03) * mm});
            skLineSegment(sketch, "E526", {"start": v(-65.11, 7259.46) * mm, "end": v(-70.55, 7260.55) * mm});
            skLineSegment(sketch, "E527", {"start": v(-2000.8, 2762.35) * mm, "end": v(-1991.75, 2740.5) * mm});
            skLineSegment(sketch, "E528", {"start": v(-2015.2, 2781.13) * mm, "end": v(-2000.8, 2762.35) * mm});
            skLineSegment(sketch, "E529", {"start": v(-36.92, 7234.74) * mm, "end": v(-39.37, 7239.71) * mm});
            skLineSegment(sketch, "E530", {"start": v(-54.89, 7255.23) * mm, "end": v(-59.86, 7257.68) * mm});
            skLineSegment(sketch, "E531", {"start": v(-59.86, 7257.68) * mm, "end": v(-65.11, 7259.46) * mm});
            skLineSegment(sketch, "E532", {"start": v(-376.05, 7259.46) * mm, "end": v(-365.08, 7260.9) * mm});
            skLineSegment(sketch, "E533", {"start": v(-150.7, 6819.93) * mm, "end": v(-126.07, 6850.93) * mm});
            skLineSegment(sketch, "E534", {"start": v(-50.28, 6859.42) * mm, "end": v(-54.89, 6856.34) * mm});
            skLineSegment(sketch, "E535", {"start": v(-365.08, 7260.9) * mm, "end": v(-70.55, 7260.55) * mm});
            skLineSegment(sketch, "E536", {"start": v(-2033.98, 2795.53) * mm, "end": v(-2015.2, 2781.13) * mm});
            skLineSegment(sketch, "E537", {"start": v(-2055.84, 2804.59) * mm, "end": v(-2033.98, 2795.53) * mm});
            skLineSegment(sketch, "E538", {"start": v(-35.13, 7229.49) * mm, "end": v(-36.92, 7234.74) * mm});
            skLineSegment(sketch, "E539", {"start": v(-1991.75, 2693.57) * mm, "end": v(-2000.8, 2671.71) * mm});
            skLineSegment(sketch, "E540", {"start": v(-65.11, 6852.1) * mm, "end": v(-70.55, 6851.02) * mm});
            skLineSegment(sketch, "E541", {"start": v(-42.45, 6867.24) * mm, "end": v(-46.1, 6863.07) * mm});
            skLineSegment(sketch, "E542", {"start": v(-46.1, 7248.5) * mm, "end": v(-50.28, 7252.15) * mm});
            skLineSegment(sketch, "E543", {"start": v(-54.89, 6856.34) * mm, "end": v(-59.86, 6853.88) * mm});
            skLineSegment(sketch, "E544", {"start": v(-46.1, 6863.07) * mm, "end": v(-50.28, 6859.42) * mm});
            skLineSegment(sketch, "E545", {"start": v(-70.55, 6851.02) * mm, "end": v(-126.07, 6850.93) * mm});
            skLineSegment(sketch, "E546", {"start": v(-42.45, 7244.32) * mm, "end": v(-46.1, 7248.5) * mm});
            skLineSegment(sketch, "E547", {"start": v(-2102.76, 2804.59) * mm, "end": v(-2079.3, 2807.67) * mm});
            skLineSegment(sketch, "E548", {"start": v(-2157.8, 2762.35) * mm, "end": v(-2143.39, 2781.13) * mm});
            skLineSegment(sketch, "E549", {"start": v(-2000.8, 2671.71) * mm, "end": v(-2015.2, 2652.94) * mm});
            skLineSegment(sketch, "E550", {"start": v(-1165.73, 5313.28) * mm, "end": v(-1150.42, 5306.93) * mm});
            skLineSegment(sketch, "E551", {"start": v(-1198.6, 5313.28) * mm, "end": v(-1182.17, 5315.44) * mm});
            skLineSegment(sketch, "E552", {"start": v(-2015.2, 2652.94) * mm, "end": v(-2033.98, 2638.54) * mm});
            skLineSegment(sketch, "E553", {"start": v(-2055.84, 2629.48) * mm, "end": v(-2079.3, 2626.4) * mm});
            skLineSegment(sketch, "E554", {"start": v(-2157.8, 2671.71) * mm, "end": v(-2166.85, 2693.57) * mm});
            skLineSegment(sketch, "E555", {"start": v(-2166.85, 2693.57) * mm, "end": v(-2169.94, 2717.03) * mm});
            skLineSegment(sketch, "E556", {"start": v(-2143.39, 2652.94) * mm, "end": v(-2157.8, 2671.71) * mm});
            skLineSegment(sketch, "E557", {"start": v(-2124.62, 2795.53) * mm, "end": v(-2102.76, 2804.59) * mm});
            skLineSegment(sketch, "E558", {"start": v(-1127.18, 5283.7) * mm, "end": v(-1120.83, 5268.38) * mm});
            skLineSegment(sketch, "E559", {"start": v(-1137.27, 5296.84) * mm, "end": v(-1127.18, 5283.7) * mm});
            skLineSegment(sketch, "E560", {"start": v(-2166.85, 2740.5) * mm, "end": v(-2157.8, 2762.35) * mm});
            skLineSegment(sketch, "E561", {"start": v(-1182.17, 5315.44) * mm, "end": v(-1165.73, 5313.28) * mm});
            skLineSegment(sketch, "E562", {"start": v(-1227.07, 5296.84) * mm, "end": v(-1213.92, 5306.93) * mm});
            skLineSegment(sketch, "E563", {"start": v(-2079.3, 2807.67) * mm, "end": v(-2055.84, 2804.59) * mm});
            skLineSegment(sketch, "E564", {"start": v(-2143.39, 2781.13) * mm, "end": v(-2124.62, 2795.53) * mm});
            skLineSegment(sketch, "E565", {"start": v(-1150.42, 5306.93) * mm, "end": v(-1137.27, 5296.84) * mm});
            skLineSegment(sketch, "E566", {"start": v(-1237.16, 5283.7) * mm, "end": v(-1227.07, 5296.84) * mm});
            skLineSegment(sketch, "E567", {"start": v(-1243.5, 5268.38) * mm, "end": v(-1237.16, 5283.7) * mm});
            skLineSegment(sketch, "E568", {"start": v(-1245.67, 5251.94) * mm, "end": v(-1243.5, 5268.38) * mm});
            skLineSegment(sketch, "E569", {"start": v(-1243.5, 5235.5) * mm, "end": v(-1245.67, 5251.94) * mm});
            skLineSegment(sketch, "E570", {"start": v(-1213.92, 5306.93) * mm, "end": v(-1198.6, 5313.28) * mm});
            skLineSegment(sketch, "E571", {"start": v(-2124.62, 2638.54) * mm, "end": v(-2143.39, 2652.94) * mm});
            skLineSegment(sketch, "E572", {"start": v(-2102.76, 2629.48) * mm, "end": v(-2124.62, 2638.54) * mm});
            skLineSegment(sketch, "E573", {"start": v(-1237.16, 5220.2) * mm, "end": v(-1243.5, 5235.5) * mm});
            skLineSegment(sketch, "E574", {"start": v(-1227.07, 5207.04) * mm, "end": v(-1237.16, 5220.2) * mm});
            skLineSegment(sketch, "E575", {"start": v(-2033.98, 2638.54) * mm, "end": v(-2055.84, 2629.48) * mm});
            skLineSegment(sketch, "E576", {"start": v(-2169.94, 2717.03) * mm, "end": v(-2166.85, 2740.5) * mm});
            skLineSegment(sketch, "E577", {"start": v(-2079.3, 2626.4) * mm, "end": v(-2102.76, 2629.48) * mm});
            skLineSegment(sketch, "E578", {"start": v(-1120.83, 5268.38) * mm, "end": v(-1118.67, 5251.94) * mm});
            skLineSegment(sketch, "E579", {"start": v(-1772.78, 7778.95) * mm, "end": v(-1789.2, 7776.79) * mm});
            skLineSegment(sketch, "E580", {"start": v(-1175.87, 7715.45) * mm, "end": v(-1178.04, 7731.89) * mm});
            skLineSegment(sketch, "E581", {"start": v(-1184.38, 7747.2) * mm, "end": v(-1194.47, 7760.35) * mm});
            skLineSegment(sketch, "E582", {"start": v(-1239.37, 7778.95) * mm, "end": v(-1772.78, 7778.95) * mm});
            skLineSegment(sketch, "E583", {"start": v(-1178.04, 7699.02) * mm, "end": v(-1175.87, 7715.45) * mm});
            skLineSegment(sketch, "E584", {"start": v(-1817.68, 7760.35) * mm, "end": v(-1827.77, 7747.2) * mm});
            skLineSegment(sketch, "E585", {"start": v(-1827.77, 7747.2) * mm, "end": v(-1834.11, 7731.89) * mm});
            skLineSegment(sketch, "E586", {"start": v(-1198.6, 5190.6) * mm, "end": v(-1213.92, 5196.95) * mm});
            skLineSegment(sketch, "E587", {"start": v(-1834.11, 7731.89) * mm, "end": v(-1836.27, 7715.45) * mm});
            skLineSegment(sketch, "E588", {"start": v(-1182.17, 5188.44) * mm, "end": v(-1198.6, 5190.6) * mm});
            skLineSegment(sketch, "E589", {"start": v(-1194.47, 7760.35) * mm, "end": v(-1207.62, 7770.44) * mm});
            skLineSegment(sketch, "E590", {"start": v(-1222.94, 7654.11) * mm, "end": v(-1207.62, 7660.46) * mm});
            skLineSegment(sketch, "E591", {"start": v(-1239.37, 7651.95) * mm, "end": v(-1222.94, 7654.11) * mm});
            skLineSegment(sketch, "E592", {"start": v(-1207.62, 7770.44) * mm, "end": v(-1222.94, 7776.79) * mm});
            skLineSegment(sketch, "E593", {"start": v(-1118.67, 5251.94) * mm, "end": v(-1120.83, 5235.5) * mm});
            skLineSegment(sketch, "E594", {"start": v(-1772.78, 7651.95) * mm, "end": v(-1239.37, 7651.95) * mm});
            skLineSegment(sketch, "E595", {"start": v(-1804.52, 7660.46) * mm, "end": v(-1789.2, 7654.11) * mm});
            skLineSegment(sketch, "E596", {"start": v(-1184.38, 7683.7) * mm, "end": v(-1178.04, 7699.02) * mm});
            skLineSegment(sketch, "E597", {"start": v(-1178.04, 7731.89) * mm, "end": v(-1184.38, 7747.2) * mm});
            skLineSegment(sketch, "E598", {"start": v(-1165.73, 5190.6) * mm, "end": v(-1182.17, 5188.44) * mm});
            skLineSegment(sketch, "E599", {"start": v(-1789.2, 7776.79) * mm, "end": v(-1804.52, 7770.44) * mm});
            skLineSegment(sketch, "E600", {"start": v(-1804.52, 7770.44) * mm, "end": v(-1817.68, 7760.35) * mm});
            skLineSegment(sketch, "E601", {"start": v(-1137.27, 5207.04) * mm, "end": v(-1150.42, 5196.95) * mm});
            skLineSegment(sketch, "E602", {"start": v(-1789.2, 7654.11) * mm, "end": v(-1772.78, 7651.95) * mm});
            skLineSegment(sketch, "E603", {"start": v(-1127.18, 5220.2) * mm, "end": v(-1137.27, 5207.04) * mm});
            skLineSegment(sketch, "E604", {"start": v(-1150.42, 5196.95) * mm, "end": v(-1165.73, 5190.6) * mm});
            skLineSegment(sketch, "E605", {"start": v(-1213.92, 5196.95) * mm, "end": v(-1227.07, 5207.04) * mm});
            skLineSegment(sketch, "E606", {"start": v(-1120.83, 5235.5) * mm, "end": v(-1127.18, 5220.2) * mm});
            skLineSegment(sketch, "E607", {"start": v(-1207.62, 7660.46) * mm, "end": v(-1194.47, 7670.55) * mm});
            skLineSegment(sketch, "E608", {"start": v(-1194.47, 7670.55) * mm, "end": v(-1184.38, 7683.7) * mm});
            skLineSegment(sketch, "E609", {"start": v(-1222.94, 7776.79) * mm, "end": v(-1239.37, 7778.95) * mm});
            skLineSegment(sketch, "E610", {"start": v(-1194.47, 7252.35) * mm, "end": v(-1207.62, 7262.44) * mm});
            skLineSegment(sketch, "E611", {"start": v(-4047.42, 5220.2) * mm, "end": v(-4053.76, 5235.5) * mm});
            skLineSegment(sketch, "E612", {"start": v(-4053.76, 5235.5) * mm, "end": v(-4055.93, 5251.94) * mm});
            skLineSegment(sketch, "E613", {"start": v(-1175.87, 7207.45) * mm, "end": v(-1178.04, 7223.89) * mm});
            skLineSegment(sketch, "E614", {"start": v(-1184.38, 7175.7) * mm, "end": v(-1178.04, 7191.02) * mm});
            skLineSegment(sketch, "E615", {"start": v(-1239.37, 7270.95) * mm, "end": v(-1772.78, 7270.95) * mm});
            skLineSegment(sketch, "E616", {"start": v(-4037.33, 5207.04) * mm, "end": v(-4047.42, 5220.2) * mm});
            skLineSegment(sketch, "E617", {"start": v(-1222.94, 7146.11) * mm, "end": v(-1207.62, 7152.46) * mm});
            skLineSegment(sketch, "E618", {"start": v(-1207.62, 7152.46) * mm, "end": v(-1194.47, 7162.55) * mm});
            skLineSegment(sketch, "E619", {"start": v(-1184.38, 7239.2) * mm, "end": v(-1194.47, 7252.35) * mm});
            skLineSegment(sketch, "E620", {"start": v(-1194.47, 7162.55) * mm, "end": v(-1184.38, 7175.7) * mm});
            skLineSegment(sketch, "E621", {"start": v(-1222.94, 7268.79) * mm, "end": v(-1239.37, 7270.95) * mm});
            skLineSegment(sketch, "E622", {"start": v(-1827.77, 7239.2) * mm, "end": v(-1834.11, 7223.89) * mm});
            skLineSegment(sketch, "E623", {"start": v(-1772.78, 7143.95) * mm, "end": v(-1239.37, 7143.95) * mm});
            skLineSegment(sketch, "E624", {"start": v(-1827.77, 7175.7) * mm, "end": v(-1817.68, 7162.55) * mm});
            skLineSegment(sketch, "E625", {"start": v(-1789.2, 7146.11) * mm, "end": v(-1772.78, 7143.95) * mm});
            skLineSegment(sketch, "E626", {"start": v(-1772.78, 7270.95) * mm, "end": v(-1789.2, 7268.79) * mm});
            skLineSegment(sketch, "E627", {"start": v(-1178.04, 7191.02) * mm, "end": v(-1175.87, 7207.45) * mm});
            skLineSegment(sketch, "E628", {"start": v(-1836.27, 7207.45) * mm, "end": v(-1834.11, 7191.02) * mm});
            skLineSegment(sketch, "E629", {"start": v(-1804.52, 7262.44) * mm, "end": v(-1817.68, 7252.35) * mm});
            skLineSegment(sketch, "E630", {"start": v(-1207.62, 7262.44) * mm, "end": v(-1222.94, 7268.79) * mm});
            skLineSegment(sketch, "E631", {"start": v(-1834.11, 7223.89) * mm, "end": v(-1836.27, 7207.45) * mm});
            skLineSegment(sketch, "E632", {"start": v(-1178.04, 7223.89) * mm, "end": v(-1184.38, 7239.2) * mm});
            skLineSegment(sketch, "E633", {"start": v(-1804.52, 7152.46) * mm, "end": v(-1789.2, 7146.11) * mm});
            skLineSegment(sketch, "E634", {"start": v(-1834.11, 7191.02) * mm, "end": v(-1827.77, 7175.7) * mm});
            skLineSegment(sketch, "E635", {"start": v(-1817.68, 7252.35) * mm, "end": v(-1827.77, 7239.2) * mm});
            skLineSegment(sketch, "E636", {"start": v(-1239.37, 7143.95) * mm, "end": v(-1222.94, 7146.11) * mm});
            skLineSegment(sketch, "E637", {"start": v(-1789.2, 6760.79) * mm, "end": v(-1804.52, 6754.44) * mm});
            skLineSegment(sketch, "E638", {"start": v(-1772.78, 6762.95) * mm, "end": v(-1789.2, 6760.79) * mm});
            skLineSegment(sketch, "E639", {"start": v(-1239.37, 6762.95) * mm, "end": v(-1772.78, 6762.95) * mm});
            skLineSegment(sketch, "E640", {"start": v(-1789.2, 7268.79) * mm, "end": v(-1804.52, 7262.44) * mm});
            skLineSegment(sketch, "E641", {"start": v(-1817.68, 7162.55) * mm, "end": v(-1804.52, 7152.46) * mm});
            skLineSegment(sketch, "E642", {"start": v(-1184.38, 6667.7) * mm, "end": v(-1178.04, 6683.02) * mm});
            skLineSegment(sketch, "E643", {"start": v(-1827.77, 6667.7) * mm, "end": v(-1817.68, 6654.55) * mm});
            skLineSegment(sketch, "E644", {"start": v(-1834.11, 6683.02) * mm, "end": v(-1827.77, 6667.7) * mm});
            skLineSegment(sketch, "E645", {"start": v(-1834.11, 6715.89) * mm, "end": v(-1836.27, 6699.45) * mm});
            skLineSegment(sketch, "E646", {"start": v(-1827.77, 6731.2) * mm, "end": v(-1834.11, 6715.89) * mm});
            skLineSegment(sketch, "E647", {"start": v(-253.72, 2740.5) * mm, "end": v(-244.67, 2762.35) * mm});
            skLineSegment(sketch, "E648", {"start": v(-1239.37, 6635.95) * mm, "end": v(-1222.94, 6638.12) * mm});
            skLineSegment(sketch, "E649", {"start": v(-1222.94, 6760.79) * mm, "end": v(-1239.37, 6762.95) * mm});
            skLineSegment(sketch, "E650", {"start": v(-1194.47, 6744.35) * mm, "end": v(-1207.62, 6754.44) * mm});
            skLineSegment(sketch, "E651", {"start": v(-1178.04, 6715.89) * mm, "end": v(-1184.38, 6731.2) * mm});
            skLineSegment(sketch, "E652", {"start": v(-1175.87, 6699.45) * mm, "end": v(-1178.04, 6715.89) * mm});
            skLineSegment(sketch, "E653", {"start": v(-1207.62, 6644.46) * mm, "end": v(-1194.47, 6654.55) * mm});
            skLineSegment(sketch, "E654", {"start": v(-1817.68, 6744.35) * mm, "end": v(-1827.77, 6731.2) * mm});
            skLineSegment(sketch, "E655", {"start": v(-230.26, 2781.13) * mm, "end": v(-211.49, 2795.53) * mm});
            skLineSegment(sketch, "E656", {"start": v(-1184.38, 6731.2) * mm, "end": v(-1194.47, 6744.35) * mm});
            skLineSegment(sketch, "E657", {"start": v(-1789.2, 6638.12) * mm, "end": v(-1772.78, 6635.95) * mm});
            skLineSegment(sketch, "E658", {"start": v(-1804.52, 6754.44) * mm, "end": v(-1817.68, 6744.35) * mm});
            skLineSegment(sketch, "E659", {"start": v(-244.67, 2762.35) * mm, "end": v(-230.26, 2781.13) * mm});
            skLineSegment(sketch, "E660", {"start": v(-189.63, 2804.59) * mm, "end": v(-166.17, 2807.67) * mm});
            skLineSegment(sketch, "E661", {"start": v(-1222.94, 6638.12) * mm, "end": v(-1207.62, 6644.46) * mm});
            skLineSegment(sketch, "E662", {"start": v(-166.17, 2807.67) * mm, "end": v(-142.71, 2804.59) * mm});
            skLineSegment(sketch, "E663", {"start": v(-142.71, 2804.59) * mm, "end": v(-120.85, 2795.53) * mm});
            skLineSegment(sketch, "E664", {"start": v(-1772.78, 6635.95) * mm, "end": v(-1239.37, 6635.95) * mm});
            skLineSegment(sketch, "E665", {"start": v(-1804.52, 6644.46) * mm, "end": v(-1789.2, 6638.12) * mm});
            skLineSegment(sketch, "E666", {"start": v(-1207.62, 6754.44) * mm, "end": v(-1222.94, 6760.79) * mm});
            skLineSegment(sketch, "E667", {"start": v(-211.49, 2795.53) * mm, "end": v(-189.63, 2804.59) * mm});
            skLineSegment(sketch, "E668", {"start": v(-1194.47, 6654.55) * mm, "end": v(-1184.38, 6667.7) * mm});
            skLineSegment(sketch, "E669", {"start": v(-1836.27, 6699.45) * mm, "end": v(-1834.11, 6683.02) * mm});
            skLineSegment(sketch, "E670", {"start": v(-1178.04, 6683.02) * mm, "end": v(-1175.87, 6699.45) * mm});
            skLineSegment(sketch, "E671", {"start": v(-256.8, 2717.03) * mm, "end": v(-253.72, 2740.5) * mm});
            skLineSegment(sketch, "E672", {"start": v(-120.85, 2795.53) * mm, "end": v(-102.08, 2781.13) * mm});
            skLineSegment(sketch, "E673", {"start": v(-1817.68, 6654.55) * mm, "end": v(-1804.52, 6644.46) * mm});
            skLineSegment(sketch, "E674", {"start": v(-1391.41, 7945.74) * mm, "end": v(-1390.33, 7951.17) * mm});
            skLineSegment(sketch, "E675", {"start": v(-1386.1, 7876.27) * mm, "end": v(-1383.01, 7871.66) * mm});
            skLineSegment(sketch, "E676", {"start": v(-87.67, 2671.71) * mm, "end": v(-102.08, 2652.94) * mm});
            skLineSegment(sketch, "E677", {"start": v(-1391.77, 7897.46) * mm, "end": v(-1390.33, 7886.5) * mm});
            skLineSegment(sketch, "E678", {"start": v(-1375.19, 7863.83) * mm, "end": v(-1370.58, 7860.75) * mm});
            skLineSegment(sketch, "E679", {"start": v(-78.62, 2693.57) * mm, "end": v(-87.67, 2671.71) * mm});
            skLineSegment(sketch, "E680", {"start": v(-1375.19, 7973.83) * mm, "end": v(-1370.58, 7976.91) * mm});
            skLineSegment(sketch, "E681", {"start": v(-78.62, 2740.5) * mm, "end": v(-75.53, 2717.03) * mm});
            skLineSegment(sketch, "E682", {"start": v(-1388.55, 7881.24) * mm, "end": v(-1386.1, 7876.27) * mm});
            skLineSegment(sketch, "E683", {"start": v(-1390.33, 7951.17) * mm, "end": v(-1388.55, 7956.43) * mm});
            skLineSegment(sketch, "E684", {"start": v(-1379.36, 7867.49) * mm, "end": v(-1375.19, 7863.83) * mm});
            skLineSegment(sketch, "E685", {"start": v(-230.26, 2652.94) * mm, "end": v(-244.67, 2671.71) * mm});
            skLineSegment(sketch, "E686", {"start": v(-1365.6, 7858.3) * mm, "end": v(-1360.36, 7856.52) * mm});
            skLineSegment(sketch, "E687", {"start": v(-142.71, 2629.48) * mm, "end": v(-166.17, 2626.4) * mm});
            skLineSegment(sketch, "E688", {"start": v(-1370.58, 7860.75) * mm, "end": v(-1365.6, 7858.3) * mm});
            skLineSegment(sketch, "E689", {"start": v(-1391.77, 7897.46) * mm, "end": v(-1391.41, 7945.74) * mm});
            skLineSegment(sketch, "E690", {"start": v(-87.67, 2762.35) * mm, "end": v(-78.62, 2740.5) * mm});
            skLineSegment(sketch, "E691", {"start": v(-102.08, 2652.94) * mm, "end": v(-120.85, 2638.54) * mm});
            skLineSegment(sketch, "E692", {"start": v(-120.85, 2638.54) * mm, "end": v(-142.71, 2629.48) * mm});
            skLineSegment(sketch, "E693", {"start": v(-189.63, 2629.48) * mm, "end": v(-211.49, 2638.54) * mm});
            skLineSegment(sketch, "E694", {"start": v(-211.49, 2638.54) * mm, "end": v(-230.26, 2652.94) * mm});
            skLineSegment(sketch, "E695", {"start": v(-253.72, 2693.57) * mm, "end": v(-256.8, 2717.03) * mm});
            skLineSegment(sketch, "E696", {"start": v(-1383.01, 7871.66) * mm, "end": v(-1379.36, 7867.49) * mm});
            skLineSegment(sketch, "E697", {"start": v(-166.17, 2626.4) * mm, "end": v(-189.63, 2629.48) * mm});
            skLineSegment(sketch, "E698", {"start": v(-244.67, 2671.71) * mm, "end": v(-253.72, 2693.57) * mm});
            skLineSegment(sketch, "E699", {"start": v(-1390.33, 7886.5) * mm, "end": v(-1388.55, 7881.24) * mm});
            skLineSegment(sketch, "E700", {"start": v(-1388.55, 7956.43) * mm, "end": v(-1386.1, 7961.4) * mm});
            skLineSegment(sketch, "E701", {"start": v(-102.08, 2781.13) * mm, "end": v(-87.67, 2762.35) * mm});
            skLineSegment(sketch, "E702", {"start": v(-1383.01, 7966) * mm, "end": v(-1379.36, 7970.18) * mm});
            skLineSegment(sketch, "E703", {"start": v(-1386.1, 7961.4) * mm, "end": v(-1383.01, 7966) * mm});
            skLineSegment(sketch, "E704", {"start": v(-1379.36, 7970.18) * mm, "end": v(-1375.19, 7973.83) * mm});
            skLineSegment(sketch, "E705", {"start": v(-75.53, 2717.03) * mm, "end": v(-78.62, 2693.57) * mm});
            skLineSegment(sketch, "E706", {"start": v(-1108.17, 7976.91) * mm, "end": v(-1113.14, 7979.37) * mm});
            skLineSegment(sketch, "E707", {"start": v(-1099.4, 7970.18) * mm, "end": v(-1103.56, 7973.83) * mm});
            skLineSegment(sketch, "E708", {"start": v(-1087.34, 7945.74) * mm, "end": v(-1088.42, 7951.17) * mm});
            skLineSegment(sketch, "E709", {"start": v(-1092.65, 7961.4) * mm, "end": v(-1095.74, 7966) * mm});
            skLineSegment(sketch, "E710", {"start": v(-1360.36, 7981.15) * mm, "end": v(-1354.92, 7982.23) * mm});
            skLineSegment(sketch, "E711", {"start": v(-1370.58, 7976.91) * mm, "end": v(-1365.6, 7979.37) * mm});
            skLineSegment(sketch, "E712", {"start": v(-2209.45, 7174.96) * mm, "end": v(-2219.54, 7161.8) * mm});
            skLineSegment(sketch, "E713", {"start": v(-1095.74, 7966) * mm, "end": v(-1099.4, 7970.18) * mm});
            skLineSegment(sketch, "E714", {"start": v(-2219.54, 7161.8) * mm, "end": v(-2232.7, 7151.72) * mm});
            skLineSegment(sketch, "E715", {"start": v(-1099.4, 7867.49) * mm, "end": v(-1103.56, 7863.83) * mm});
            skLineSegment(sketch, "E716", {"start": v(-1090.2, 7881.24) * mm, "end": v(-1092.65, 7876.27) * mm});
            skLineSegment(sketch, "E717", {"start": v(-1103.56, 7863.83) * mm, "end": v(-1108.17, 7860.75) * mm});
            skLineSegment(sketch, "E718", {"start": v(-1113.14, 7979.37) * mm, "end": v(-1118.4, 7981.15) * mm});
            skLineSegment(sketch, "E719", {"start": v(-1088.42, 7951.17) * mm, "end": v(-1090.2, 7956.43) * mm});
            skLineSegment(sketch, "E720", {"start": v(-2647.3, 6410.8) * mm, "end": v(-2633.93, 6400.55) * mm});
            skLineSegment(sketch, "E721", {"start": v(-1354.92, 7982.23) * mm, "end": v(-1123.83, 7982.23) * mm});
            skLineSegment(sketch, "E722", {"start": v(-2633.93, 6400.55) * mm, "end": v(-2623.68, 6387.18) * mm});
            skLineSegment(sketch, "E723", {"start": v(-1087.34, 7945.74) * mm, "end": v(-1087.34, 7891.93) * mm});
            skLineSegment(sketch, "E724", {"start": v(-1103.56, 7973.83) * mm, "end": v(-1108.17, 7976.91) * mm});
            skLineSegment(sketch, "E725", {"start": v(-1087.34, 7891.93) * mm, "end": v(-1088.42, 7886.5) * mm});
            skLineSegment(sketch, "E726", {"start": v(-1088.42, 7886.5) * mm, "end": v(-1090.2, 7881.24) * mm});
            skLineSegment(sketch, "E727", {"start": v(-1108.17, 7860.75) * mm, "end": v(-1113.14, 7858.3) * mm});
            skLineSegment(sketch, "E728", {"start": v(-1118.4, 7981.15) * mm, "end": v(-1123.83, 7982.23) * mm});
            skLineSegment(sketch, "E729", {"start": v(-1092.65, 7876.27) * mm, "end": v(-1095.74, 7871.66) * mm});
            skLineSegment(sketch, "E730", {"start": v(-1090.2, 7956.43) * mm, "end": v(-1092.65, 7961.4) * mm});
            skLineSegment(sketch, "E731", {"start": v(-1118.4, 7856.52) * mm, "end": v(-1123.83, 7855.44) * mm});
            skLineSegment(sketch, "E732", {"start": v(-1123.83, 7855.44) * mm, "end": v(-1148.47, 7855.34) * mm});
            skLineSegment(sketch, "E733", {"start": v(-2203.1, 7190.27) * mm, "end": v(-2209.45, 7174.96) * mm});
            skLineSegment(sketch, "E734", {"start": v(-1113.14, 7858.3) * mm, "end": v(-1118.4, 7856.52) * mm});
            skLineSegment(sketch, "E735", {"start": v(-1365.6, 7979.37) * mm, "end": v(-1360.36, 7981.15) * mm});
            skLineSegment(sketch, "E736", {"start": v(-1095.74, 7871.66) * mm, "end": v(-1099.4, 7867.49) * mm});
            skLineSegment(sketch, "E737", {"start": v(-1360.36, 7856.52) * mm, "end": v(-1349.38, 7855.07) * mm});
            skLineSegment(sketch, "E738", {"start": v(-2647.3, 6070.45) * mm, "end": v(-2662.85, 6064) * mm});
            skLineSegment(sketch, "E739", {"start": v(-2679.55, 6061.81) * mm, "end": v(-2696.25, 6064) * mm});
            skLineSegment(sketch, "E740", {"start": v(-2617.23, 6371.62) * mm, "end": v(-2615.03, 6354.93) * mm});
            skLineSegment(sketch, "E741", {"start": v(-2696.25, 6064) * mm, "end": v(-2711.8, 6070.45) * mm});
            skLineSegment(sketch, "E742", {"start": v(-2617.23, 6109.63) * mm, "end": v(-2623.68, 6094.07) * mm});
            skLineSegment(sketch, "E743", {"start": v(-2735.42, 6094.07) * mm, "end": v(-2741.87, 6109.63) * mm});
            skLineSegment(sketch, "E744", {"start": v(-2623.68, 6387.18) * mm, "end": v(-2617.23, 6371.62) * mm});
            skLineSegment(sketch, "E745", {"start": v(-2711.8, 6410.8) * mm, "end": v(-2696.25, 6417.24) * mm});
            skLineSegment(sketch, "E746", {"start": v(-2633.93, 5200.55) * mm, "end": v(-2623.68, 5187.19) * mm});
            skLineSegment(sketch, "E747", {"start": v(-2615.03, 4926.33) * mm, "end": v(-2617.23, 4909.63) * mm});
            skLineSegment(sketch, "E748", {"start": v(-2633.93, 4880.71) * mm, "end": v(-2647.3, 4870.46) * mm});
            skLineSegment(sketch, "E749", {"start": v(-2354.77, 5926.18) * mm, "end": v(-2304.31, 5991.94) * mm});
            skLineSegment(sketch, "E750", {"start": v(-2304.31, 5991.94) * mm, "end": v(-2238.56, 6042.4) * mm});
            skLineSegment(sketch, "E751", {"start": v(-2711.8, 6070.45) * mm, "end": v(-2725.17, 6080.7) * mm});
            skLineSegment(sketch, "E752", {"start": v(-2696.25, 6417.24) * mm, "end": v(-2679.55, 6419.44) * mm});
            skLineSegment(sketch, "E753", {"start": v(-2397.3, 5767.43) * mm, "end": v(-2386.49, 5849.6) * mm});
            skLineSegment(sketch, "E754", {"start": v(-2623.68, 6094.07) * mm, "end": v(-2633.93, 6080.7) * mm});
            skLineSegment(sketch, "E755", {"start": v(-2615.03, 5154.93) * mm, "end": v(-2615.03, 4926.33) * mm});
            skLineSegment(sketch, "E756", {"start": v(-2696.25, 4864.01) * mm, "end": v(-2711.8, 4870.46) * mm});
            skLineSegment(sketch, "E757", {"start": v(-2386.49, 5849.6) * mm, "end": v(-2354.77, 5926.18) * mm});
            skLineSegment(sketch, "E758", {"start": v(-2238.56, 6042.4) * mm, "end": v(-2161.98, 6074.11) * mm});
            skLineSegment(sketch, "E759", {"start": v(-2161.98, 6074.11) * mm, "end": v(-2079.8, 6084.93) * mm});
            skLineSegment(sketch, "E760", {"start": v(-2615.03, 6126.33) * mm, "end": v(-2617.23, 6109.63) * mm});
            skLineSegment(sketch, "E761", {"start": v(-2633.93, 6080.7) * mm, "end": v(-2647.3, 6070.45) * mm});
            skLineSegment(sketch, "E762", {"start": v(-2615.03, 6354.93) * mm, "end": v(-2615.03, 6126.33) * mm});
            skLineSegment(sketch, "E763", {"start": v(-2662.85, 6064) * mm, "end": v(-2679.55, 6061.81) * mm});
            skLineSegment(sketch, "E764", {"start": v(-2741.87, 6371.62) * mm, "end": v(-2735.42, 6387.18) * mm});
            skLineSegment(sketch, "E765", {"start": v(-2741.87, 6109.63) * mm, "end": v(-2744.06, 6126.33) * mm});
            skLineSegment(sketch, "E766", {"start": v(-2744.06, 6126.33) * mm, "end": v(-2744.06, 6354.93) * mm});
            skLineSegment(sketch, "E767", {"start": v(-2735.42, 6387.18) * mm, "end": v(-2725.17, 6400.55) * mm});
            skLineSegment(sketch, "E768", {"start": v(-2623.68, 4894.07) * mm, "end": v(-2633.93, 4880.71) * mm});
            skLineSegment(sketch, "E769", {"start": v(-2725.17, 6080.7) * mm, "end": v(-2735.42, 6094.07) * mm});
            skLineSegment(sketch, "E770", {"start": v(-2079.8, 5195.93) * mm, "end": v(-2161.98, 5206.75) * mm});
            skLineSegment(sketch, "E771", {"start": v(-2386.49, 5431.26) * mm, "end": v(-2397.3, 5513.43) * mm});
            skLineSegment(sketch, "E772", {"start": v(-1511.81, 5210.8) * mm, "end": v(-1496.25, 5217.25) * mm});
            skLineSegment(sketch, "E773", {"start": v(-1423.68, 4894.07) * mm, "end": v(-1433.94, 4880.71) * mm});
            skLineSegment(sketch, "E774", {"start": v(-1433.94, 4880.71) * mm, "end": v(-1447.3, 4870.46) * mm});
            skLineSegment(sketch, "E775", {"start": v(-1855.3, 5288.92) * mm, "end": v(-1921.06, 5238.47) * mm});
            skLineSegment(sketch, "E776", {"start": v(-1762.3, 5513.43) * mm, "end": v(-1773.12, 5431.26) * mm});
            skLineSegment(sketch, "E777", {"start": v(-1773.12, 5431.26) * mm, "end": v(-1804.84, 5354.68) * mm});
            skLineSegment(sketch, "E778", {"start": v(-1855.3, 5991.94) * mm, "end": v(-1804.84, 5926.18) * mm});
            skLineSegment(sketch, "E779", {"start": v(-1544.07, 5154.93) * mm, "end": v(-1541.87, 5171.63) * mm});
            skLineSegment(sketch, "E780", {"start": v(-1423.68, 6387.18) * mm, "end": v(-1417.24, 6371.62) * mm});
            skLineSegment(sketch, "E781", {"start": v(-1921.06, 6042.4) * mm, "end": v(-1855.3, 5991.94) * mm});
            skLineSegment(sketch, "E782", {"start": v(-1525.17, 5200.55) * mm, "end": v(-1511.81, 5210.8) * mm});
            skLineSegment(sketch, "E783", {"start": v(-1496.25, 5217.25) * mm, "end": v(-1479.55, 5219.45) * mm});
            skLineSegment(sketch, "E784", {"start": v(-1462.86, 5217.25) * mm, "end": v(-1447.3, 5210.8) * mm});
            skLineSegment(sketch, "E785", {"start": v(-2079.8, 6084.93) * mm, "end": v(-1997.63, 6074.11) * mm});
            skLineSegment(sketch, "E786", {"start": v(-1921.06, 5238.47) * mm, "end": v(-1997.63, 5206.75) * mm});
            skLineSegment(sketch, "E787", {"start": v(-1535.43, 5187.19) * mm, "end": v(-1525.17, 5200.55) * mm});
            skLineSegment(sketch, "E788", {"start": v(-1433.94, 5200.55) * mm, "end": v(-1423.68, 5187.19) * mm});
            skLineSegment(sketch, "E789", {"start": v(-1423.68, 5187.19) * mm, "end": v(-1417.24, 5171.63) * mm});
            skLineSegment(sketch, "E790", {"start": v(-1997.63, 5206.75) * mm, "end": v(-2079.8, 5195.93) * mm});
            skLineSegment(sketch, "E791", {"start": v(-1417.24, 5171.63) * mm, "end": v(-1415.04, 5154.93) * mm});
            skLineSegment(sketch, "E792", {"start": v(-1417.24, 4909.63) * mm, "end": v(-1423.68, 4894.07) * mm});
            skLineSegment(sketch, "E793", {"start": v(-1773.12, 5849.6) * mm, "end": v(-1762.3, 5767.43) * mm});
            skLineSegment(sketch, "E794", {"start": v(-2304.31, 5288.92) * mm, "end": v(-2354.77, 5354.68) * mm});
            skLineSegment(sketch, "E795", {"start": v(-1541.87, 6109.63) * mm, "end": v(-1544.07, 6126.33) * mm});
            skLineSegment(sketch, "E796", {"start": v(-1447.3, 5210.8) * mm, "end": v(-1433.94, 5200.55) * mm});
            skLineSegment(sketch, "E797", {"start": v(-1804.84, 5926.18) * mm, "end": v(-1773.12, 5849.6) * mm});
            skLineSegment(sketch, "E798", {"start": v(-1762.3, 5767.43) * mm, "end": v(-1762.3, 5513.43) * mm});
            skLineSegment(sketch, "E799", {"start": v(-1804.84, 5354.68) * mm, "end": v(-1855.3, 5288.92) * mm});
            skLineSegment(sketch, "E800", {"start": v(-1997.63, 6074.11) * mm, "end": v(-1921.06, 6042.4) * mm});
            skLineSegment(sketch, "E801", {"start": v(-2354.77, 5354.68) * mm, "end": v(-2386.49, 5431.26) * mm});
            skLineSegment(sketch, "E802", {"start": v(-1511.81, 4870.46) * mm, "end": v(-1525.17, 4880.71) * mm});
            skLineSegment(sketch, "E803", {"start": v(-1462.86, 4864.01) * mm, "end": v(-1479.55, 4861.82) * mm});
            skLineSegment(sketch, "E804", {"start": v(-1496.25, 4864.01) * mm, "end": v(-1511.81, 4870.46) * mm});
            skLineSegment(sketch, "E805", {"start": v(-1479.55, 4861.82) * mm, "end": v(-1496.25, 4864.01) * mm});
            skLineSegment(sketch, "E806", {"start": v(-1447.3, 4870.46) * mm, "end": v(-1462.86, 4864.01) * mm});
            skLineSegment(sketch, "E807", {"start": v(-34.05, 6887.52) * mm, "end": v(-34.05, 7224.05) * mm});
            skLineSegment(sketch, "E808", {"start": v(-169.28, 6775.02) * mm, "end": v(-159.2, 6788.18) * mm});
            skLineSegment(sketch, "E809", {"start": v(-269.18, 6788.13) * mm, "end": v(-259.09, 6774.99) * mm});
            skLineSegment(sketch, "E810", {"start": v(-1148.47, 7855.34) * mm, "end": v(-1349.38, 7855.07) * mm});
            skSolve(sketch);
        }
        {
            var Q0;
            Q0 = qSketchRegion(id + "F0", true);
            extrude(context, id + "F1", {"entities" : qUnion([Q0]), "depth" : 12.7 * mm});
        }
    });
